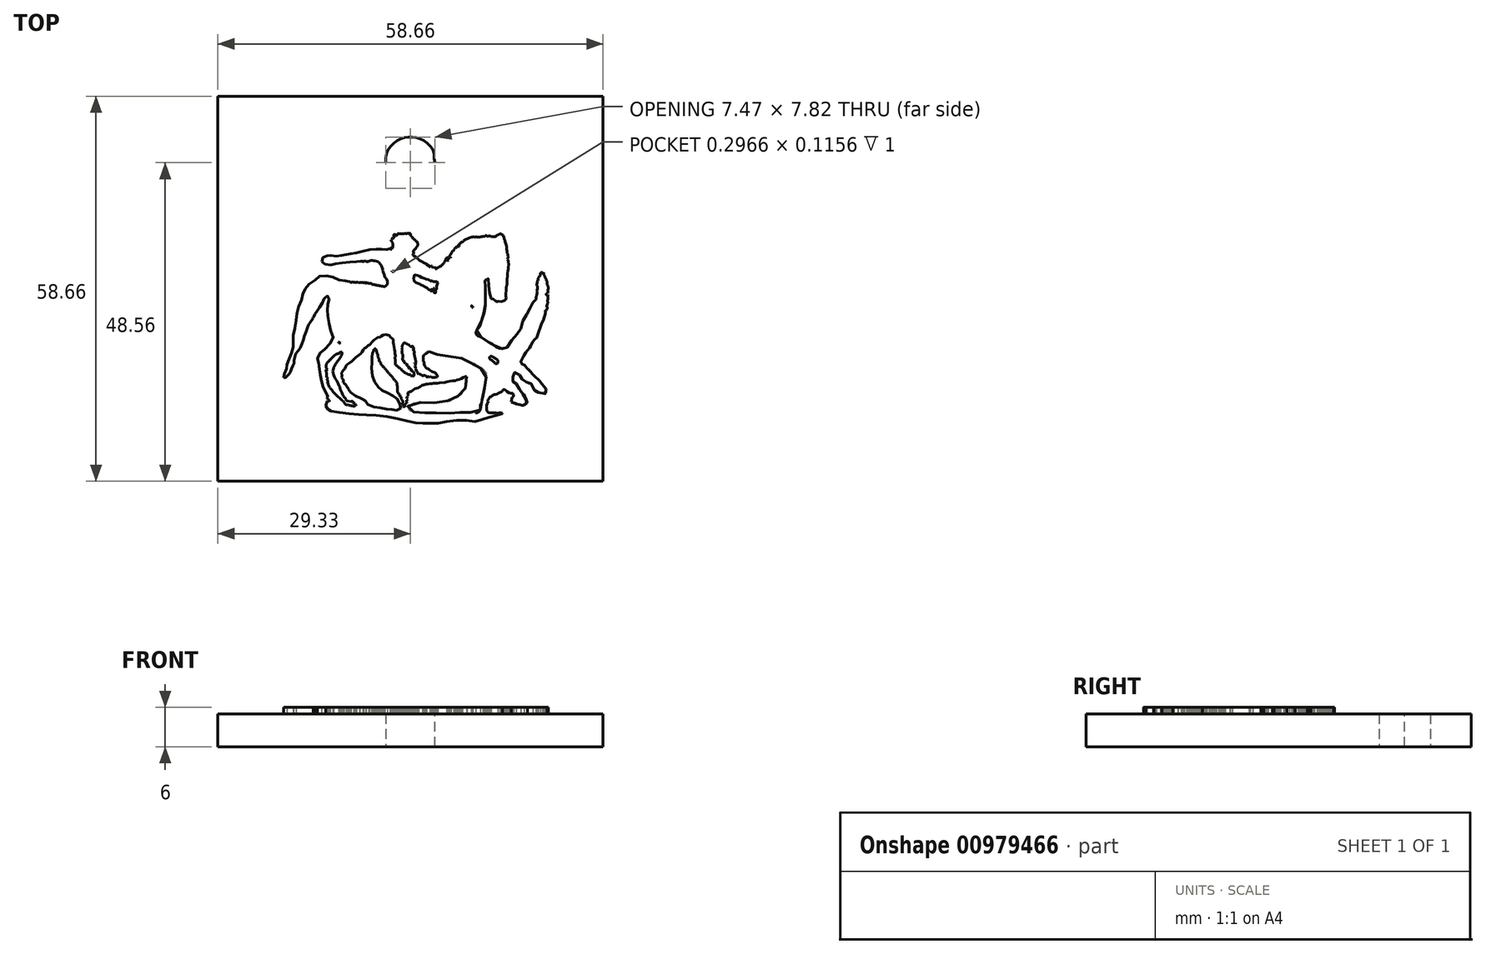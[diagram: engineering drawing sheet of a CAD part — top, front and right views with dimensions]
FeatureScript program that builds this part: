
annotation { "Feature Type Name" : "Feature", "Feature Type Description" : "" }
export const myFeature = defineFeature(function(context is Context, id is Id, definition is map)
    precondition{}
    {
        {
            var Q0;
            Q0=qCreatedBy(makeId("Top.planeOp"),FACE);
            var sketch = newSketch(context, id + "F0", { "sketchPlane" : qUnion([Q0])});
            skLineSegment(sketch, "E0", {"start": v(29.33, 29.33) * mm, "end": v(-29.33, 29.33) * mm});
            skLineSegment(sketch, "E1", {"start": v(-29.33, 29.33) * mm, "end": v(-29.33, -29.33) * mm});
            skLineSegment(sketch, "E2", {"start": v(-29.33, -29.33) * mm, "end": v(29.33, -29.33) * mm});
            skLineSegment(sketch, "E3", {"start": v(29.33, -29.33) * mm, "end": v(29.33, 29.33) * mm});
            skLineSegment(sketch, "E4", {"start": v(14, -19.04) * mm, "end": v(14, -19) * mm});
            skLineSegment(sketch, "E5", {"start": v(11.06, 7.86) * mm, "end": v(11.06, 8) * mm});
            skLineSegment(sketch, "E6", {"start": v(3.86, 3) * mm, "end": v(3.86, 3.18) * mm});
            skLineSegment(sketch, "E7", {"start": v(-7.23, 4.19) * mm, "end": v(-7.23, 4.11) * mm});
            skLineSegment(sketch, "E8", {"start": v(-7.15, 0.98) * mm, "end": v(-7.73, 0.98) * mm});
            skLineSegment(sketch, "E9", {"start": v(1.24, -12.84) * mm, "end": v(1.24, -13.05) * mm});
            skFitSpline(sketch, "E10", {"points": [v(3.73, 19.23) * mm, v(3.63, 18.57) * mm, v(3.43, 17.28) * mm, v(1.94, 15.85) * mm, v(0, 15.32) * mm, v(-1.96, 15.85) * mm, v(-3.38, 17.28) * mm, v(-3.73, 18.57) * mm, v(-3.73, 19.23) * mm, v(-3.73, 19.23) * mm]});
            skFitSpline(sketch, "E11", {"points": [v(-3.73, 19.23) * mm, v(-3.73, 19.89) * mm, v(-3.38, 21.18) * mm, v(-1.96, 22.61) * mm, v(0, 23.14) * mm, v(1.94, 22.61) * mm, v(3.43, 21.18) * mm, v(3.63, 19.89) * mm, v(3.73, 19.23) * mm]});
            skFitSpline(sketch, "E12", {"points": [v(-12.55, -16.47) * mm, v(-12.57, -16.49) * mm, v(-12.62, -16.51) * mm, v(-12.68, -16.56) * mm, v(-12.72, -16.58) * mm, v(-12.75, -16.6) * mm]});
            skFitSpline(sketch, "E13", {"points": [v(-12.75, -16.6) * mm, v(-12.72, -16.63) * mm, v(-12.67, -16.68) * mm, v(-12.6, -16.76) * mm, v(-12.56, -16.8) * mm, v(-12.54, -16.83) * mm]});
            skFitSpline(sketch, "E14", {"points": [v(-12.54, -16.83) * mm, v(-12.55, -16.85) * mm, v(-12.56, -16.88) * mm, v(-12.58, -16.92) * mm, v(-12.6, -16.95) * mm, v(-12.6, -16.96) * mm]});
            skFitSpline(sketch, "E15", {"points": [v(-12.6, -16.96) * mm, v(-12.57, -16.97) * mm, v(-12.5, -16.99) * mm, v(-12.41, -17) * mm, v(-12.35, -17.02) * mm, v(-12.31, -17.03) * mm]});
            skFitSpline(sketch, "E16", {"points": [v(-12.31, -17.03) * mm, v(-12.32, -17.06) * mm, v(-12.33, -17.11) * mm, v(-12.48, -17.1) * mm, v(-12.56, -17.07) * mm, v(-12.63, -17.05) * mm]});
            skFitSpline(sketch, "E17", {"points": [v(-12.63, -17.05) * mm, v(-12.69, -17.14) * mm, v(-12.8, -17.3) * mm, v(-12.87, -17.61) * mm, v(-12.9, -17.83) * mm, v(-12.87, -17.96) * mm, v(-12.85, -18) * mm, v(-12.8, -18.06) * mm, v(-12.74, -18.16) * mm, v(-12.65, -18.28) * mm, v(-12.58, -18.37) * mm, v(-12.53, -18.43) * mm, v(-12.51, -18.46) * mm, v(-12.43, -18.5) * mm, v(-12.26, -18.57) * mm, v(-12.04, -18.7) * mm, v(-11.65, -18.78) * mm, v(-11.1, -18.82) * mm, v(-10.4, -18.94) * mm, v(-9.72, -19.03) * mm, v(-9.05, -19.1) * mm, v(-8.38, -19.14) * mm, v(-7.79, -19.18) * mm, v(-7.27, -19.2) * mm, v(-6.82, -19.22) * mm, v(-6.25, -19.25) * mm, v(-5.58, -19.3) * mm, v(-4.8, -19.37) * mm, v(-3.99, -19.46) * mm, v(-3.15, -19.6) * mm, v(-2.29, -19.75) * mm, v(-1.49, -19.96) * mm, v(-0.74, -20.15) * mm, v(-0.04, -20.3) * mm, v(0.46, -20.43) * mm, v(0.78, -20.48) * mm, v(0.9, -20.48) * mm, v(1.22, -20.48) * mm, v(1.74, -20.48) * mm, v(2.46, -20.49) * mm, v(3, -20.49) * mm, v(3.37, -20.5) * mm, v(3.55, -20.52) * mm, v(3.84, -20.55) * mm, v(4.25, -20.53) * mm, v(4.75, -20.43) * mm, v(5.33, -20.3) * mm, v(6, -20.19) * mm, v(6.76, -20.06) * mm, v(7.48, -20.05) * mm, v(8.15, -20.07) * mm, v(8.78, -20.05) * mm, v(9.34, -20.14) * mm, v(9.82, -20.24) * mm, v(10.24, -20.2) * mm, v(10.61, -20.08) * mm, v(10.95, -19.92) * mm, v(11.28, -19.8) * mm, v(11.65, -19.68) * mm, v(12.08, -19.57) * mm, v(12.56, -19.46) * mm, v(12.98, -19.36) * mm, v(13.36, -19.25) * mm, v(13.68, -19.15) * mm, v(13.9, -19.08) * mm, v(14, -19.04) * mm]});
            skFitSpline(sketch, "E18", {"points": [v(14, -19) * mm, v(13.99, -19) * mm, v(13.96, -18.98) * mm, v(13.91, -18.96) * mm, v(13.72, -18.94) * mm, v(13.4, -18.96) * mm, v(12.92, -18.94) * mm, v(12.44, -18.94) * mm, v(11.97, -18.9) * mm, v(11.64, -18.53) * mm, v(11.59, -18.12) * mm, v(11.62, -17.76) * mm, v(11.73, -17.48) * mm, v(11.8, -17.3) * mm, v(11.84, -17.15) * mm, v(11.83, -17.1) * mm, v(11.86, -17.04) * mm, v(11.83, -17.04) * mm, v(11.81, -17.03) * mm, v(11.8, -17.03) * mm, v(11.8, -17.03) * mm]});
            skFitSpline(sketch, "E19", {"points": [v(11.8, -17.03) * mm, v(11.82, -16.98) * mm, v(11.88, -16.9) * mm, v(11.96, -16.75) * mm, v(12.04, -16.62) * mm, v(12.15, -16.52) * mm, v(12.25, -16.45) * mm, v(12.34, -16.38) * mm, v(12.4, -16.33) * mm, v(12.45, -16.29) * mm, v(12.5, -16.25) * mm, v(12.57, -16.21) * mm, v(12.65, -16.17) * mm, v(12.79, -16.15) * mm, v(12.97, -16.14) * mm, v(13.19, -16.04) * mm, v(13.4, -15.94) * mm, v(13.6, -15.86) * mm, v(13.77, -15.75) * mm, v(13.9, -15.7) * mm, v(13.99, -15.64) * mm, v(14, -15.6) * mm, v(14.03, -15.55) * mm, v(14.06, -15.47) * mm, v(14.14, -15.39) * mm, v(14.24, -15.35) * mm, v(14.34, -15.36) * mm, v(14.43, -15.41) * mm, v(14.57, -15.52) * mm, v(14.77, -15.7) * mm, v(15.05, -15.9) * mm, v(15.34, -15.94) * mm, v(15.58, -15.96) * mm, v(15.7, -16.15) * mm, v(15.7, -16.29) * mm, v(15.7, -16.37) * mm]});
            skFitSpline(sketch, "E20", {"points": [v(15.7, -16.37) * mm, v(15.7, -16.37) * mm, v(15.7, -16.37) * mm, v(15.68, -16.36) * mm, v(15.65, -16.35) * mm, v(15.65, -16.43) * mm, v(15.63, -16.48) * mm, v(15.61, -16.53) * mm, v(15.6, -16.56) * mm, v(15.59, -16.58) * mm, v(15.57, -16.6) * mm, v(15.54, -16.6) * mm, v(15.52, -16.6) * mm, v(15.5, -16.6) * mm, v(15.49, -16.6) * mm]});
            skFitSpline(sketch, "E21", {"points": [v(15.49, -16.6) * mm, v(15.47, -16.67) * mm, v(15.43, -16.82) * mm, v(15.38, -17.06) * mm, v(15.35, -17.21) * mm, v(15.33, -17.3) * mm]});
            skFitSpline(sketch, "E22", {"points": [v(15.33, -17.3) * mm, v(15.39, -17.3) * mm, v(15.51, -17.33) * mm, v(15.7, -17.36) * mm, v(15.92, -17.44) * mm, v(16.16, -17.57) * mm, v(16.46, -17.66) * mm, v(16.7, -17.7) * mm, v(16.91, -17.72) * mm, v(17.05, -17.76) * mm, v(17.2, -17.76) * mm, v(17.33, -17.72) * mm, v(17.44, -17.65) * mm, v(17.54, -17.61) * mm, v(17.58, -17.56) * mm, v(17.6, -17.54) * mm, v(17.62, -17.5) * mm, v(17.69, -17.46) * mm, v(17.76, -17.41) * mm, v(17.81, -17.34) * mm, v(17.8, -17.25) * mm, v(17.75, -17.17) * mm, v(17.68, -17.03) * mm, v(17.62, -16.82) * mm, v(17.51, -16.56) * mm, v(17.44, -16.36) * mm, v(17.38, -16.23) * mm, v(17.33, -16.16) * mm, v(17.2, -16.06) * mm, v(17, -15.92) * mm, v(16.8, -15.64) * mm, v(16.7, -15.42) * mm, v(16.61, -15.27) * mm, v(16.56, -15.2) * mm, v(16.44, -15.1) * mm, v(16.28, -14.98) * mm, v(16.1, -14.76) * mm, v(16.13, -14.55) * mm, v(16.07, -14.44) * mm, v(16.03, -14.41) * mm, v(15.95, -14.39) * mm, v(15.84, -14.4) * mm, v(15.73, -14.32) * mm, v(15.65, -14.24) * mm, v(15.6, -14.15) * mm, v(15.55, -14.08) * mm, v(15.48, -13.98) * mm, v(15.4, -13.84) * mm, v(15.42, -13.62) * mm, v(15.54, -13.49) * mm, v(15.64, -13.36) * mm, v(15.7, -13.24) * mm, v(15.76, -13.12) * mm, v(15.8, -13.01) * mm, v(15.82, -12.9) * mm, v(15.86, -12.78) * mm, v(15.96, -12.66) * mm, v(16.13, -12.63) * mm, v(16.31, -12.75) * mm, v(16.46, -12.95) * mm, v(16.66, -13.18) * mm, v(16.81, -13.35) * mm, v(16.9, -13.47) * mm, v(16.95, -13.55) * mm, v(16.97, -13.64) * mm, v(17, -13.72) * mm, v(17.06, -13.78) * mm, v(17.13, -13.82) * mm, v(17.2, -13.84) * mm, v(17.26, -13.88) * mm, v(17.37, -13.95) * mm, v(17.5, -14.07) * mm, v(17.68, -14.22) * mm, v(17.8, -14.34) * mm, v(17.91, -14.41) * mm, v(17.98, -14.44) * mm, v(18.14, -14.46) * mm, v(18.4, -14.47) * mm, v(18.63, -14.72) * mm, v(18.72, -14.96) * mm, v(18.78, -15.18) * mm, v(18.81, -15.35) * mm, v(18.84, -15.5) * mm, v(18.87, -15.6) * mm, v(18.93, -15.68) * mm, v(19.08, -15.72) * mm, v(19.3, -15.77) * mm, v(19.57, -15.86) * mm, v(19.82, -15.98) * mm, v(20.08, -16.07) * mm, v(20.36, -16.05) * mm, v(20.57, -16) * mm, v(20.75, -15.94) * mm, v(20.8, -15.8) * mm, v(20.8, -15.62) * mm, v(20.76, -15.41) * mm, v(20.61, -15.22) * mm, v(20.43, -15.1) * mm, v(20.25, -14.94) * mm, v(20.12, -14.75) * mm, v(20.05, -14.58) * mm, v(19.99, -14.45) * mm, v(19.92, -14.37) * mm, v(19.85, -14.27) * mm, v(19.76, -14.17) * mm, v(19.66, -14.05) * mm, v(19.57, -13.95) * mm, v(19.5, -13.87) * mm, v(19.43, -13.81) * mm, v(19.31, -13.7) * mm, v(19.16, -13.54) * mm, v(18.95, -13.34) * mm, v(18.73, -13.07) * mm, v(18.46, -12.76) * mm, v(18.11, -12.44) * mm, v(17.84, -12.18) * mm, v(17.64, -11.95) * mm, v(17.5, -11.78) * mm, v(17.4, -11.66) * mm, v(17.36, -11.6) * mm]});
            skFitSpline(sketch, "E23", {"points": [v(17.36, -11.6) * mm, v(17.3, -11.61) * mm, v(17.18, -11.64) * mm, v(17.03, -11.52) * mm, v(16.92, -11.39) * mm, v(16.83, -11.24) * mm, v(16.82, -11.07) * mm, v(16.87, -10.92) * mm, v(16.95, -10.8) * mm, v(17.03, -10.67) * mm, v(17.15, -10.48) * mm, v(17.3, -10.23) * mm, v(17.48, -9.9) * mm, v(17.6, -9.68) * mm, v(17.69, -9.54) * mm, v(17.71, -9.5) * mm, v(17.81, -9.42) * mm, v(17.98, -9.33) * mm, v(18.11, -9.1) * mm, v(18.22, -8.95) * mm, v(18.3, -8.86) * mm, v(18.32, -8.81) * mm, v(18.38, -8.66) * mm, v(18.47, -8.39) * mm, v(18.68, -8.06) * mm, v(18.84, -7.8) * mm, v(18.99, -7.66) * mm, v(19.08, -7.62) * mm, v(19.16, -7.57) * mm, v(19.21, -7.5) * mm, v(19.24, -7.44) * mm, v(19.28, -7.36) * mm, v(19.3, -7.24) * mm, v(19.34, -7.1) * mm, v(19.42, -6.86) * mm, v(19.55, -6.5) * mm, v(19.72, -6.01) * mm, v(19.86, -5.63) * mm, v(19.97, -5.36) * mm, v(20.06, -5.2) * mm, v(20.17, -5.03) * mm, v(20.27, -4.85) * mm, v(20.33, -4.63) * mm, v(20.36, -4.45) * mm, v(20.4, -4.29) * mm, v(20.46, -4.16) * mm, v(20.5, -4.04) * mm, v(20.56, -3.94) * mm, v(20.64, -3.82) * mm, v(20.54, -3.76) * mm, v(20.55, -3.7) * mm, v(20.56, -3.68) * mm, v(20.57, -3.64) * mm, v(20.58, -3.6) * mm, v(20.6, -3.58) * mm, v(20.58, -3.5) * mm, v(20.45, -3.42) * mm, v(20.6, -3.35) * mm, v(20.7, -3.3) * mm, v(20.75, -3.17) * mm, v(20.82, -3.08) * mm, v(20.87, -2.96) * mm, v(20.84, -2.85) * mm, v(20.77, -2.75) * mm, v(20.75, -2.68) * mm, v(20.74, -2.65) * mm]});
            skFitSpline(sketch, "E24", {"points": [v(20.74, -2.65) * mm, v(20.75, -2.6) * mm, v(20.78, -2.52) * mm, v(20.82, -2.4) * mm, v(20.84, -2.32) * mm, v(20.86, -2.27) * mm]});
            skFitSpline(sketch, "E25", {"points": [v(20.86, -2.27) * mm, v(20.87, -2.27) * mm, v(20.9, -2.26) * mm, v(20.93, -2.25) * mm, v(20.95, -2.24) * mm, v(20.96, -2.23) * mm]});
            skFitSpline(sketch, "E26", {"points": [v(20.96, -2.23) * mm, v(20.96, -2.22) * mm, v(20.95, -2.19) * mm, v(20.94, -2.15) * mm, v(20.93, -2.09) * mm, v(20.92, -2.01) * mm, v(20.9, -1.92) * mm, v(20.9, -1.8) * mm, v(20.93, -1.64) * mm, v(20.94, -1.46) * mm, v(20.97, -1.32) * mm, v(20.96, -1.22) * mm, v(20.94, -1.16) * mm, v(20.92, -1.1) * mm, v(20.92, -1.04) * mm, v(20.92, -0.97) * mm, v(20.92, -0.93) * mm, v(20.92, -0.9) * mm]});
            skFitSpline(sketch, "E27", {"points": [v(20.92, -0.9) * mm, v(20.91, -0.92) * mm, v(20.9, -0.95) * mm, v(20.87, -1) * mm, v(20.85, -1.02) * mm, v(20.85, -1.03) * mm]});
            skFitSpline(sketch, "E28", {"points": [v(20.85, -1.03) * mm, v(20.8, -1) * mm, v(20.73, -0.93) * mm, v(20.73, -0.77) * mm, v(20.78, -0.69) * mm, v(20.8, -0.64) * mm]});
            skFitSpline(sketch, "E29", {"points": [v(20.8, -0.64) * mm, v(20.82, -0.65) * mm, v(20.85, -0.65) * mm, v(20.9, -0.67) * mm, v(20.95, -0.68) * mm, v(20.97, -0.7) * mm]});
            skFitSpline(sketch, "E30", {"points": [v(20.97, -0.7) * mm, v(20.97, -0.66) * mm, v(20.97, -0.59) * mm, v(20.96, -0.48) * mm, v(20.96, -0.35) * mm, v(20.97, -0.2) * mm, v(20.99, -0.03) * mm, v(21, 0.11) * mm, v(21, 0.22) * mm, v(20.99, 0.29) * mm, v(20.94, 0.41) * mm, v(20.88, 0.6) * mm, v(20.83, 0.87) * mm, v(20.84, 1.07) * mm, v(20.8, 1.2) * mm, v(20.75, 1.24) * mm, v(20.72, 1.28) * mm, v(20.7, 1.3) * mm]});
            skFitSpline(sketch, "E31", {"points": [v(20.7, 1.3) * mm, v(20.7, 1.32) * mm, v(20.7, 1.37) * mm, v(20.67, 1.44) * mm, v(20.63, 1.56) * mm, v(20.55, 1.72) * mm, v(20.44, 1.93) * mm, v(20.39, 2.08) * mm, v(20.34, 2.16) * mm, v(20.32, 2.17) * mm, v(20.29, 2.22) * mm, v(20.36, 2.35) * mm, v(20.18, 2.38) * mm, v(20.14, 2.46) * mm, v(20.12, 2.5) * mm]});
            skFitSpline(sketch, "E32", {"points": [v(20.12, 2.5) * mm, v(20.1, 2.5) * mm, v(20.05, 2.49) * mm, v(19.97, 2.48) * mm, v(19.9, 2.46) * mm, v(19.86, 2.42) * mm, v(19.83, 2.38) * mm, v(19.8, 2.36) * mm, v(19.8, 2.34) * mm]});
            skFitSpline(sketch, "E33", {"points": [v(19.8, 2.34) * mm, v(19.8, 2.3) * mm, v(19.82, 2.2) * mm, v(19.77, 2.04) * mm, v(19.7, 1.94) * mm, v(19.63, 1.88) * mm, v(19.58, 1.83) * mm, v(19.55, 1.74) * mm, v(19.5, 1.63) * mm, v(19.42, 1.48) * mm, v(19.47, 1.37) * mm, v(19.5, 1.32) * mm]});
            skFitSpline(sketch, "E34", {"points": [v(19.5, 1.32) * mm, v(19.48, 1.3) * mm, v(19.45, 1.26) * mm, v(19.34, 1.22) * mm, v(19.4, 1.17) * mm, v(19.44, 1.14) * mm]});
            skFitSpline(sketch, "E35", {"points": [v(19.44, 1.14) * mm, v(19.4, 1.1) * mm, v(19.33, 1.02) * mm, v(19.29, 0.86) * mm, v(19.28, 0.73) * mm, v(19.26, 0.64) * mm, v(19.25, 0.58) * mm, v(19.25, 0.51) * mm, v(19.28, 0.44) * mm, v(19.33, 0.36) * mm, v(19.36, 0.24) * mm, v(19.35, 0.1) * mm, v(19.34, -0.07) * mm, v(19.33, -0.2) * mm, v(19.33, -0.29) * mm, v(19.33, -0.34) * mm, v(19.33, -0.4) * mm, v(19.33, -0.46) * mm, v(19.32, -0.53) * mm, v(19.3, -0.64) * mm, v(19.27, -0.77) * mm, v(19.24, -0.93) * mm, v(19.2, -1.05) * mm, v(19.2, -1.14) * mm, v(19.18, -1.18) * mm, v(19.16, -1.24) * mm, v(19.12, -1.29) * mm, v(19.09, -1.37) * mm, v(19.14, -1.44) * mm, v(19.16, -1.52) * mm, v(19.14, -1.58) * mm, v(19.12, -1.63) * mm, v(19.1, -1.65) * mm]});
            skFitSpline(sketch, "E36", {"points": [v(19.1, -1.65) * mm, v(19.08, -1.68) * mm, v(19.04, -1.73) * mm, v(18.96, -1.82) * mm, v(18.9, -1.9) * mm, v(18.84, -1.95) * mm, v(18.8, -2) * mm, v(18.75, -2.03) * mm, v(18.72, -2.06) * mm, v(18.7, -2.09) * mm, v(18.68, -2.15) * mm, v(18.7, -2.25) * mm, v(18.63, -2.36) * mm, v(18.52, -2.5) * mm, v(18.4, -2.7) * mm, v(18.26, -2.96) * mm, v(18.13, -3.19) * mm, v(18.01, -3.37) * mm, v(17.9, -3.52) * mm, v(17.8, -3.68) * mm, v(17.72, -3.85) * mm, v(17.64, -4.03) * mm, v(17.54, -4.22) * mm, v(17.42, -4.43) * mm, v(17.3, -4.65) * mm, v(17.17, -4.86) * mm, v(17.04, -5.06) * mm, v(16.96, -5.28) * mm, v(16.92, -5.53) * mm, v(16.9, -5.81) * mm, v(16.8, -6.12) * mm, v(16.62, -6.3) * mm, v(16.5, -6.44) * mm, v(16.46, -6.56) * mm, v(16.39, -6.69) * mm, v(16.28, -6.83) * mm, v(16.16, -7) * mm, v(15.98, -7.17) * mm, v(15.76, -7.37) * mm, v(15.56, -7.63) * mm, v(15.4, -7.94) * mm, v(15.25, -8.25) * mm, v(15.06, -8.54) * mm, v(14.92, -8.78) * mm, v(14.77, -8.92) * mm, v(14.63, -8.96) * mm, v(14.51, -9) * mm, v(14.4, -9.05) * mm, v(14.28, -9.07) * mm, v(14.18, -9.09) * mm, v(14.1, -9.1) * mm, v(14.02, -9.11) * mm, v(13.82, -9.1) * mm, v(13.51, -9.04) * mm, v(13.1, -8.88) * mm, v(12.83, -8.68) * mm, v(12.63, -8.54) * mm, v(12.5, -8.47) * mm, v(12.37, -8.4) * mm, v(12.25, -8.33) * mm, v(12.13, -8.27) * mm, v(11.92, -8.13) * mm, v(11.63, -7.93) * mm, v(11.23, -7.68) * mm, v(10.95, -7.47) * mm, v(10.75, -7.37) * mm, v(10.66, -7.34) * mm, v(10.44, -7.28) * mm, v(10.15, -7.08) * mm, v(9.98, -6.62) * mm, v(10.17, -6.2) * mm, v(10.46, -5.86) * mm, v(10.65, -5.47) * mm, v(10.8, -5.12) * mm, v(10.88, -4.81) * mm, v(10.94, -4.56) * mm, v(11.02, -4.26) * mm, v(11.12, -3.94) * mm, v(11.23, -3.58) * mm, v(11.32, -3.24) * mm, v(11.37, -2.92) * mm, v(11.4, -2.62) * mm, v(11.44, -2.24) * mm, v(11.46, -1.76) * mm, v(11.42, -1.19) * mm, v(11.4, -0.76) * mm, v(11.43, -0.49) * mm, v(11.46, -0.36) * mm, v(11.47, -0.21) * mm, v(11.47, -0.05) * mm, v(11.46, 0.14) * mm, v(11.44, 0.33) * mm, v(11.41, 0.54) * mm, v(11.38, 0.76) * mm, v(11.35, 0.95) * mm, v(11.34, 1.1) * mm, v(11.33, 1.23) * mm, v(11.32, 1.36) * mm, v(11.34, 1.5) * mm, v(11.43, 1.64) * mm, v(11.57, 1.7) * mm, v(11.71, 1.68) * mm, v(11.83, 1.57) * mm, v(11.87, 1.4) * mm, v(11.88, 1.2) * mm, v(11.89, 1) * mm, v(11.9, 0.8) * mm, v(11.93, 0.64) * mm, v(11.97, 0.5) * mm, v(12, 0.3) * mm, v(12, 0.05) * mm, v(12.02, -0.25) * mm, v(12.04, -0.53) * mm, v(12.09, -0.78) * mm, v(12.14, -1) * mm, v(12.18, -1.18) * mm, v(12.22, -1.32) * mm, v(12.27, -1.43) * mm, v(12.3, -1.5) * mm, v(12.3, -1.55) * mm]});
            skFitSpline(sketch, "E37", {"points": [v(12.3, -1.55) * mm, v(12.4, -1.56) * mm, v(12.57, -1.57) * mm, v(12.8, -1.72) * mm, v(12.95, -1.86) * mm, v(13.07, -1.96) * mm, v(13.16, -1.98) * mm, v(13.25, -1.95) * mm, v(13.34, -1.92) * mm, v(13.42, -1.9) * mm, v(13.56, -1.93) * mm, v(13.74, -1.96) * mm, v(13.96, -1.92) * mm, v(14.15, -1.87) * mm, v(14.3, -1.83) * mm, v(14.4, -1.75) * mm, v(14.46, -1.65) * mm, v(14.52, -1.54) * mm, v(14.57, -1.43) * mm, v(14.58, -1.32) * mm, v(14.55, -1.23) * mm, v(14.52, -1.16) * mm, v(14.51, -0.98) * mm, v(14.55, -0.71) * mm, v(14.56, -0.35) * mm, v(14.6, 0) * mm, v(14.64, 0.32) * mm, v(14.69, 0.63) * mm, v(14.73, 0.89) * mm, v(14.74, 1.11) * mm, v(14.73, 1.3) * mm, v(14.74, 1.52) * mm, v(14.76, 1.77) * mm, v(14.78, 2.05) * mm, v(14.8, 2.3) * mm, v(14.82, 2.5) * mm, v(14.84, 2.67) * mm, v(14.86, 2.81) * mm, v(14.88, 2.93) * mm, v(14.9, 3.03) * mm, v(14.9, 3.15) * mm, v(14.92, 3.3) * mm, v(14.95, 3.5) * mm, v(14.95, 3.7) * mm, v(14.92, 3.93) * mm, v(14.87, 4.18) * mm, v(14.85, 4.34) * mm, v(14.83, 4.43) * mm]});
            skFitSpline(sketch, "E38", {"points": [v(14.83, 4.43) * mm, v(14.84, 4.44) * mm, v(14.86, 4.46) * mm, v(14.89, 4.5) * mm, v(14.91, 4.52) * mm, v(14.92, 4.54) * mm]});
            skFitSpline(sketch, "E39", {"points": [v(14.92, 4.54) * mm, v(14.9, 4.54) * mm, v(14.87, 4.55) * mm, v(14.82, 4.57) * mm, v(14.78, 4.57) * mm, v(14.77, 4.58) * mm]});
            skFitSpline(sketch, "E40", {"points": [v(14.77, 4.58) * mm, v(14.78, 4.59) * mm, v(14.8, 4.6) * mm, v(14.81, 4.64) * mm, v(14.85, 4.69) * mm, v(14.9, 4.77) * mm, v(14.87, 4.88) * mm, v(14.81, 4.92) * mm, v(14.78, 4.94) * mm]});
            skFitSpline(sketch, "E41", {"points": [v(14.78, 4.94) * mm, v(14.8, 5) * mm, v(14.84, 5.12) * mm, v(14.82, 5.3) * mm, v(14.73, 5.43) * mm, v(14.7, 5.55) * mm, v(14.72, 5.63) * mm, v(14.73, 5.75) * mm, v(14.7, 5.9) * mm, v(14.68, 6.08) * mm, v(14.68, 6.28) * mm, v(14.65, 6.5) * mm, v(14.57, 6.75) * mm, v(14.51, 6.94) * mm, v(14.47, 7.09) * mm, v(14.44, 7.18) * mm, v(14.43, 7.28) * mm, v(14.4, 7.39) * mm, v(14.34, 7.49) * mm, v(14.31, 7.56) * mm, v(14.28, 7.6) * mm, v(14.27, 7.6) * mm, v(14.23, 7.67) * mm, v(14.29, 7.81) * mm, v(14.15, 7.96) * mm, v(14.13, 8.08) * mm, v(14.1, 8.15) * mm, v(14.09, 8.17) * mm, v(14.04, 8.2) * mm, v(13.95, 8.25) * mm, v(13.82, 8.3) * mm, v(13.76, 8.38) * mm, v(13.7, 8.41) * mm, v(13.66, 8.41) * mm, v(13.63, 8.41) * mm, v(13.62, 8.41) * mm]});
            skFitSpline(sketch, "E42", {"points": [v(13.62, 8.41) * mm, v(13.6, 8.37) * mm, v(13.57, 8.3) * mm, v(13.45, 8.27) * mm, v(13.33, 8.23) * mm, v(13.23, 8.17) * mm, v(13.12, 8.1) * mm, v(13.07, 8) * mm, v(12.96, 7.94) * mm, v(12.85, 7.95) * mm, v(12.75, 7.94) * mm, v(12.67, 7.94) * mm, v(12.62, 7.94) * mm, v(12.54, 7.93) * mm, v(12.43, 7.92) * mm, v(12.31, 8.01) * mm, v(12.3, 8.1) * mm, v(12.29, 8.15) * mm]});
            skFitSpline(sketch, "E43", {"points": [v(12.29, 8.15) * mm, v(12.27, 8.13) * mm, v(12.23, 8.09) * mm, v(12.17, 8.02) * mm, v(12.13, 7.98) * mm, v(12.11, 7.95) * mm]});
            skFitSpline(sketch, "E44", {"points": [v(12.11, 7.95) * mm, v(12.09, 7.99) * mm, v(12.04, 8.05) * mm, v(11.91, 8.06) * mm, v(11.85, 8) * mm, v(11.79, 7.98) * mm, v(11.76, 7.99) * mm, v(11.7, 8.01) * mm, v(11.63, 8.05) * mm, v(11.54, 8.1) * mm, v(11.48, 8.13) * mm, v(11.45, 8.15) * mm]});
            skFitSpline(sketch, "E45", {"points": [v(11.45, 8.15) * mm, v(11.44, 8.1) * mm, v(11.43, 8.03) * mm, v(11.31, 7.98) * mm, v(11.25, 8.03) * mm, v(11.21, 8.05) * mm]});
            skFitSpline(sketch, "E46", {"points": [v(11.21, 8.05) * mm, v(11.2, 8.03) * mm, v(11.17, 8) * mm, v(11.12, 7.93) * mm, v(11.08, 7.89) * mm, v(11.06, 7.86) * mm]});
            skFitSpline(sketch, "E47", {"points": [v(11.06, 8) * mm, v(11.02, 8) * mm, v(10.93, 7.95) * mm, v(10.8, 7.97) * mm, v(10.7, 7.9) * mm, v(10.62, 7.88) * mm, v(10.57, 7.9) * mm, v(10.5, 7.9) * mm, v(10.44, 7.89) * mm, v(10.38, 7.88) * mm, v(10.33, 7.87) * mm, v(10.28, 7.87) * mm, v(10.25, 7.87) * mm, v(10.2, 7.9) * mm, v(10.13, 7.92) * mm, v(10.03, 7.94) * mm, v(9.97, 7.9) * mm, v(9.91, 7.87) * mm, v(9.88, 7.88) * mm, v(9.8, 7.9) * mm, v(9.69, 7.9) * mm, v(9.53, 7.92) * mm, v(9.43, 7.87) * mm, v(9.37, 7.85) * mm, v(9.34, 7.86) * mm, v(9.24, 7.86) * mm, v(9.06, 7.81) * mm, v(8.8, 7.72) * mm, v(8.63, 7.6) * mm, v(8.48, 7.53) * mm, v(8.37, 7.5) * mm, v(8.29, 7.47) * mm, v(8.23, 7.44) * mm, v(8.2, 7.42) * mm, v(8.18, 7.4) * mm, v(8.15, 7.36) * mm, v(8.12, 7.33) * mm, v(8.08, 7.28) * mm, v(8.03, 7.24) * mm, v(7.96, 7.18) * mm, v(7.92, 7.15) * mm, v(7.9, 7.13) * mm]});
            skFitSpline(sketch, "E48", {"points": [v(7.9, 7.13) * mm, v(7.9, 7.12) * mm, v(7.9, 7.11) * mm, v(7.91, 7.1) * mm, v(7.93, 7.06) * mm, v(7.87, 7.1) * mm, v(7.84, 7.12) * mm, v(7.8, 7.14) * mm, v(7.8, 7.14) * mm]});
            skFitSpline(sketch, "E49", {"points": [v(7.8, 7.14) * mm, v(7.77, 7.13) * mm, v(7.73, 7.1) * mm, v(7.67, 7.05) * mm, v(7.63, 6.99) * mm, v(7.63, 6.9) * mm, v(7.56, 6.91) * mm, v(7.53, 6.9) * mm, v(7.51, 6.9) * mm]});
            skFitSpline(sketch, "E50", {"points": [v(7.51, 6.9) * mm, v(7.5, 6.86) * mm, v(7.47, 6.75) * mm, v(7.44, 6.6) * mm, v(7.41, 6.49) * mm, v(7.4, 6.44) * mm]});
            skFitSpline(sketch, "E51", {"points": [v(7.4, 6.44) * mm, v(7.4, 6.44) * mm, v(7.38, 6.44) * mm, v(7.36, 6.44) * mm, v(7.34, 6.44) * mm, v(7.33, 6.44) * mm]});
            skFitSpline(sketch, "E52", {"points": [v(7.33, 6.44) * mm, v(7.33, 6.46) * mm, v(7.32, 6.5) * mm, v(7.3, 6.56) * mm, v(7.31, 6.64) * mm, v(7.28, 6.63) * mm, v(7.28, 6.63) * mm, v(7.26, 6.63) * mm, v(7.27, 6.6) * mm, v(7.26, 6.57) * mm, v(7.26, 6.55) * mm, v(7.25, 6.54) * mm]});
            skFitSpline(sketch, "E53", {"points": [v(7.25, 6.54) * mm, v(7.24, 6.53) * mm, v(7.21, 6.53) * mm, v(7.18, 6.53) * mm, v(7.15, 6.53) * mm, v(7.14, 6.53) * mm]});
            skFitSpline(sketch, "E54", {"points": [v(7.14, 6.53) * mm, v(7.12, 6.46) * mm, v(7.09, 6.32) * mm, v(6.88, 6.27) * mm, v(6.79, 6.19) * mm, v(6.74, 6.14) * mm]});
            skFitSpline(sketch, "E55", {"points": [v(6.74, 6.14) * mm, v(6.74, 6.14) * mm, v(6.74, 6.12) * mm, v(6.75, 6.08) * mm, v(6.75, 6.06) * mm, v(6.76, 6.04) * mm]});
            skFitSpline(sketch, "E56", {"points": [v(6.76, 6.04) * mm, v(6.74, 6.04) * mm, v(6.7, 6.05) * mm, v(6.64, 6.05) * mm, v(6.6, 6.06) * mm, v(6.58, 6.06) * mm]});
            skFitSpline(sketch, "E57", {"points": [v(6.58, 6.06) * mm, v(6.6, 6.04) * mm, v(6.62, 6.01) * mm, v(6.65, 5.97) * mm, v(6.67, 5.94) * mm, v(6.68, 5.92) * mm]});
            skFitSpline(sketch, "E58", {"points": [v(6.68, 5.92) * mm, v(6.64, 5.89) * mm, v(6.56, 5.81) * mm, v(6.44, 5.7) * mm, v(6.35, 5.62) * mm, v(6.3, 5.58) * mm]});
            skFitSpline(sketch, "E59", {"points": [v(6.3, 5.58) * mm, v(6.3, 5.53) * mm, v(6.3, 5.46) * mm, v(6.23, 5.37) * mm, v(6.17, 5.37) * mm, v(6.14, 5.37) * mm]});
            skFitSpline(sketch, "E60", {"points": [v(6.14, 5.37) * mm, v(6.14, 5.32) * mm, v(6.14, 5.22) * mm, v(6.02, 5.12) * mm, v(6, 5.03) * mm, v(5.98, 4.98) * mm]});
            skFitSpline(sketch, "E61", {"points": [v(5.98, 4.98) * mm, v(6, 4.98) * mm, v(6.03, 4.97) * mm, v(6.1, 4.94) * mm, v(6.14, 4.93) * mm, v(6.16, 4.92) * mm]});
            skFitSpline(sketch, "E62", {"points": [v(6.16, 4.92) * mm, v(6.15, 4.9) * mm, v(6.13, 4.85) * mm, v(6.1, 4.78) * mm, v(6.08, 4.73) * mm, v(6.07, 4.7) * mm]});
            skFitSpline(sketch, "E63", {"points": [v(6.07, 4.7) * mm, v(6.05, 4.73) * mm, v(6.02, 4.78) * mm, v(5.97, 4.85) * mm, v(5.94, 4.9) * mm, v(5.92, 4.92) * mm]});
            skFitSpline(sketch, "E64", {"points": [v(5.92, 4.92) * mm, v(5.92, 4.85) * mm, v(5.93, 4.71) * mm, v(5.83, 4.54) * mm, v(5.75, 4.44) * mm, v(5.7, 4.4) * mm]});
            skFitSpline(sketch, "E65", {"points": [v(5.7, 4.4) * mm, v(5.72, 4.39) * mm, v(5.75, 4.37) * mm, v(5.8, 4.33) * mm, v(5.82, 4.31) * mm, v(5.83, 4.3) * mm]});
            skFitSpline(sketch, "E66", {"points": [v(5.83, 4.3) * mm, v(5.76, 4.3) * mm, v(5.65, 4.28) * mm, v(5.55, 4.44) * mm, v(5.66, 4.53) * mm, v(5.68, 4.63) * mm, v(5.67, 4.7) * mm, v(5.66, 4.75) * mm, v(5.66, 4.78) * mm]});
            skFitSpline(sketch, "E67", {"points": [v(5.66, 4.78) * mm, v(5.6, 4.73) * mm, v(5.48, 4.63) * mm, v(5.38, 4.43) * mm, v(5.28, 4.2) * mm, v(5.14, 3.98) * mm, v(4.95, 3.76) * mm, v(4.8, 3.57) * mm, v(4.63, 3.44) * mm, v(4.48, 3.38) * mm, v(4.35, 3.31) * mm, v(4.24, 3.25) * mm, v(4.15, 3.2) * mm, v(4.09, 3.17) * mm, v(4.06, 3.15) * mm]});
            skFitSpline(sketch, "E68", {"points": [v(4.06, 3.15) * mm, v(4.07, 3.14) * mm, v(4.08, 3.13) * mm, v(4.1, 3.1) * mm, v(4.13, 3.08) * mm, v(4.13, 3.07) * mm]});
            skFitSpline(sketch, "E69", {"points": [v(4.13, 3.07) * mm, v(4.1, 3.08) * mm, v(4.04, 3.1) * mm, v(3.9, 3.14) * mm, v(3.9, 3.04) * mm, v(3.9, 2.98) * mm]});
            skFitSpline(sketch, "E70", {"points": [v(3.9, 2.98) * mm, v(3.9, 2.98) * mm, v(3.89, 2.99) * mm, v(3.87, 2.99) * mm, v(3.86, 3) * mm, v(3.86, 3) * mm]});
            skFitSpline(sketch, "E71", {"points": [v(3.86, 3.18) * mm, v(3.85, 3.19) * mm, v(3.82, 3.2) * mm, v(3.77, 3.23) * mm, v(3.73, 3.25) * mm, v(3.7, 3.26) * mm]});
            skFitSpline(sketch, "E72", {"points": [v(3.7, 3.26) * mm, v(3.7, 3.26) * mm, v(3.68, 3.24) * mm, v(3.65, 3.2) * mm, v(3.62, 3.18) * mm, v(3.6, 3.17) * mm]});
            skFitSpline(sketch, "E73", {"points": [v(3.6, 3.17) * mm, v(3.6, 3.19) * mm, v(3.59, 3.22) * mm, v(3.57, 3.27) * mm, v(3.55, 3.3) * mm, v(3.55, 3.33) * mm]});
            skFitSpline(sketch, "E74", {"points": [v(3.55, 3.33) * mm, v(3.53, 3.31) * mm, v(3.5, 3.29) * mm, v(3.46, 3.25) * mm, v(3.43, 3.23) * mm, v(3.42, 3.21) * mm]});
            skFitSpline(sketch, "E75", {"points": [v(3.42, 3.21) * mm, v(3.42, 3.23) * mm, v(3.43, 3.26) * mm, v(3.43, 3.3) * mm, v(3.44, 3.33) * mm, v(3.44, 3.34) * mm]});
            skFitSpline(sketch, "E76", {"points": [v(3.44, 3.34) * mm, v(3.41, 3.34) * mm, v(3.37, 3.32) * mm, v(3.25, 3.33) * mm, v(3.28, 3.42) * mm, v(3.3, 3.48) * mm]});
            skFitSpline(sketch, "E77", {"points": [v(3.3, 3.48) * mm, v(3.3, 3.48) * mm, v(3.28, 3.48) * mm, v(3.26, 3.48) * mm, v(3.24, 3.48) * mm, v(3.24, 3.48) * mm]});
            skFitSpline(sketch, "E78", {"points": [v(3.24, 3.48) * mm, v(3.22, 3.46) * mm, v(3.2, 3.42) * mm, v(3.14, 3.36) * mm, v(3.11, 3.32) * mm, v(3.1, 3.3) * mm]});
            skFitSpline(sketch, "E79", {"points": [v(3.1, 3.3) * mm, v(3.02, 3.34) * mm, v(2.87, 3.44) * mm, v(2.63, 3.59) * mm, v(2.48, 3.69) * mm, v(2.4, 3.74) * mm]});
            skFitSpline(sketch, "E80", {"points": [v(2.4, 3.74) * mm, v(2.4, 3.75) * mm, v(2.42, 3.78) * mm, v(2.43, 3.8) * mm, v(2.46, 3.85) * mm, v(2.42, 3.83) * mm, v(2.4, 3.82) * mm, v(2.34, 3.82) * mm, v(2.26, 3.86) * mm, v(2.13, 3.9) * mm, v(2, 3.98) * mm, v(1.84, 4.1) * mm, v(1.62, 4.17) * mm, v(1.46, 4.28) * mm, v(1.33, 4.37) * mm, v(1.23, 4.44) * mm, v(1.18, 4.54) * mm, v(1.13, 4.63) * mm, v(1.05, 4.67) * mm, v(0.97, 4.72) * mm, v(0.87, 4.78) * mm, v(0.76, 4.85) * mm, v(0.7, 4.9) * mm, v(0.65, 4.91) * mm]});
            skFitSpline(sketch, "E81", {"points": [v(0.65, 4.91) * mm, v(0.66, 4.93) * mm, v(0.66, 4.95) * mm, v(0.67, 5) * mm, v(0.68, 5.05) * mm, v(0.69, 5.07) * mm]});
            skFitSpline(sketch, "E82", {"points": [v(0.69, 5.07) * mm, v(0.66, 5.04) * mm, v(0.61, 4.98) * mm, v(0.5, 5) * mm, v(0.46, 5.07) * mm, v(0.4, 5.14) * mm, v(0.36, 5.21) * mm, v(0.33, 5.26) * mm, v(0.31, 5.3) * mm]});
            skFitSpline(sketch, "E83", {"points": [v(0.31, 5.3) * mm, v(0.33, 5.3) * mm, v(0.37, 5.3) * mm, v(0.43, 5.32) * mm, v(0.46, 5.33) * mm, v(0.48, 5.33) * mm]});
            skFitSpline(sketch, "E84", {"points": [v(0.48, 5.33) * mm, v(0.48, 5.35) * mm, v(0.48, 5.38) * mm, v(0.47, 5.44) * mm, v(0.48, 5.5) * mm, v(0.5, 5.55) * mm, v(0.5, 5.62) * mm, v(0.45, 5.66) * mm, v(0.45, 5.73) * mm, v(0.47, 5.8) * mm, v(0.57, 5.92) * mm, v(0.76, 6.06) * mm, v(0.93, 6.34) * mm, v(1.1, 6.54) * mm, v(1.17, 6.74) * mm, v(1.12, 6.89) * mm, v(1.08, 7) * mm, v(1.05, 7.09) * mm, v(1.02, 7.15) * mm, v(1, 7.2) * mm, v(1, 7.22) * mm]});
            skFitSpline(sketch, "E85", {"points": [v(1, 7.22) * mm, v(0.99, 7.2) * mm, v(0.98, 7.2) * mm, v(0.97, 7.17) * mm, v(0.97, 7.15) * mm, v(0.96, 7.14) * mm]});
            skFitSpline(sketch, "E86", {"points": [v(0.96, 7.14) * mm, v(0.9, 7.2) * mm, v(0.8, 7.33) * mm, v(0.63, 7.53) * mm, v(0.47, 7.58) * mm, v(0.39, 7.6) * mm]});
            skFitSpline(sketch, "E87", {"points": [v(0.39, 7.6) * mm, v(0.4, 7.62) * mm, v(0.42, 7.65) * mm, v(0.46, 7.7) * mm, v(0.48, 7.74) * mm, v(0.5, 7.76) * mm]});
            skFitSpline(sketch, "E88", {"points": [v(0.5, 7.76) * mm, v(0.46, 7.75) * mm, v(0.39, 7.74) * mm, v(0.28, 7.79) * mm, v(0.23, 7.9) * mm, v(0.17, 8) * mm, v(0.08, 8.08) * mm, v(0.02, 8.15) * mm, v(-0.01, 8.18) * mm]});
            skFitSpline(sketch, "E89", {"points": [v(-0.01, 8.18) * mm, v(0, 8.2) * mm, v(0.01, 8.24) * mm, v(0.04, 8.3) * mm, v(0.05, 8.36) * mm, v(0.06, 8.38) * mm]});
            skFitSpline(sketch, "E90", {"points": [v(0.06, 8.38) * mm, v(-0.01, 8.4) * mm, v(-0.18, 8.47) * mm, v(-0.45, 8.46) * mm, v(-0.61, 8.39) * mm, v(-0.69, 8.35) * mm]});
            skFitSpline(sketch, "E91", {"points": [v(-0.69, 8.35) * mm, v(-0.72, 8.4) * mm, v(-0.78, 8.46) * mm, v(-0.91, 8.41) * mm, v(-1.03, 8.38) * mm, v(-1.18, 8.38) * mm, v(-1.33, 8.35) * mm, v(-1.46, 8.39) * mm, v(-1.57, 8.4) * mm, v(-1.67, 8.39) * mm, v(-1.74, 8.38) * mm, v(-1.77, 8.37) * mm]});
            skFitSpline(sketch, "E92", {"points": [v(-1.77, 8.37) * mm, v(-1.78, 8.38) * mm, v(-1.78, 8.4) * mm, v(-1.79, 8.45) * mm, v(-1.8, 8.49) * mm, v(-1.8, 8.5) * mm]});
            skFitSpline(sketch, "E93", {"points": [v(-1.8, 8.5) * mm, v(-1.82, 8.47) * mm, v(-1.87, 8.4) * mm, v(-1.93, 8.3) * mm, v(-2, 8.22) * mm, v(-2.03, 8.15) * mm, v(-2.1, 8.12) * mm, v(-2.15, 8.19) * mm, v(-2.2, 8.24) * mm, v(-2.25, 8.29) * mm, v(-2.29, 8.32) * mm, v(-2.3, 8.33) * mm]});
            skFitSpline(sketch, "E94", {"points": [v(-2.3, 8.33) * mm, v(-2.32, 8.33) * mm, v(-2.36, 8.31) * mm, v(-2.42, 8.29) * mm, v(-2.47, 8.27) * mm, v(-2.5, 8.26) * mm]});
            skFitSpline(sketch, "E95", {"points": [v(-2.5, 8.26) * mm, v(-2.52, 8.22) * mm, v(-2.56, 8.14) * mm, v(-2.47, 8.02) * mm, v(-2.4, 8) * mm, v(-2.35, 7.99) * mm]});
            skFitSpline(sketch, "E96", {"points": [v(-2.35, 7.99) * mm, v(-2.38, 7.96) * mm, v(-2.44, 7.9) * mm, v(-2.54, 7.82) * mm, v(-2.6, 7.76) * mm, v(-2.63, 7.74) * mm]});
            skFitSpline(sketch, "E97", {"points": [v(-2.63, 7.74) * mm, v(-2.63, 7.73) * mm, v(-2.62, 7.72) * mm, v(-2.61, 7.7) * mm, v(-2.6, 7.68) * mm, v(-2.65, 7.72) * mm, v(-2.68, 7.73) * mm, v(-2.7, 7.74) * mm, v(-2.72, 7.75) * mm]});
            skFitSpline(sketch, "E98", {"points": [v(-2.72, 7.75) * mm, v(-2.74, 7.73) * mm, v(-2.77, 7.7) * mm, v(-2.82, 7.63) * mm, v(-2.86, 7.6) * mm, v(-2.88, 7.57) * mm]});
            skFitSpline(sketch, "E99", {"points": [v(-2.88, 7.57) * mm, v(-2.87, 7.56) * mm, v(-2.86, 7.54) * mm, v(-2.85, 7.51) * mm, v(-2.83, 7.49) * mm, v(-2.83, 7.48) * mm]});
            skFitSpline(sketch, "E100", {"points": [v(-2.83, 7.48) * mm, v(-2.87, 7.45) * mm, v(-2.94, 7.42) * mm, v(-2.94, 7.28) * mm, v(-2.82, 7.17) * mm, v(-2.73, 7) * mm, v(-2.68, 6.79) * mm, v(-2.7, 6.63) * mm, v(-2.7, 6.5) * mm, v(-2.69, 6.42) * mm, v(-2.68, 6.36) * mm, v(-2.67, 6.33) * mm]});
            skFitSpline(sketch, "E101", {"points": [v(-2.67, 6.33) * mm, v(-2.68, 6.32) * mm, v(-2.7, 6.3) * mm, v(-2.72, 6.26) * mm, v(-2.74, 6.22) * mm, v(-2.76, 6.2) * mm]});
            skFitSpline(sketch, "E102", {"points": [v(-2.76, 6.2) * mm, v(-2.76, 6.24) * mm, v(-2.79, 6.3) * mm, v(-2.95, 6.21) * mm, v(-3.03, 6.14) * mm, v(-3.1, 6.1) * mm]});
            skFitSpline(sketch, "E103", {"points": [v(-3.1, 6.1) * mm, v(-3.07, 6.1) * mm, v(-3.02, 6.12) * mm, v(-2.95, 6.14) * mm, v(-2.9, 6.16) * mm, v(-2.88, 6.16) * mm]});
            skFitSpline(sketch, "E104", {"points": [v(-2.88, 6.16) * mm, v(-2.87, 6.14) * mm, v(-2.85, 6.1) * mm, v(-2.82, 6.02) * mm, v(-2.8, 5.97) * mm, v(-2.8, 5.94) * mm]});
            skFitSpline(sketch, "E105", {"points": [v(-2.8, 5.94) * mm, v(-2.8, 5.94) * mm, v(-2.85, 5.94) * mm, v(-2.9, 5.94) * mm, v(-2.97, 5.94) * mm, v(-3.04, 6) * mm, v(-3.17, 6.1) * mm, v(-3.23, 5.95) * mm, v(-3.29, 5.97) * mm, v(-3.31, 5.99) * mm, v(-3.4, 6) * mm, v(-3.56, 5.97) * mm, v(-3.76, 6.03) * mm, v(-3.98, 6.04) * mm, v(-4.2, 6.02) * mm, v(-4.42, 6.01) * mm, v(-4.67, 6) * mm, v(-4.95, 6) * mm, v(-5.26, 6.01) * mm, v(-5.62, 6) * mm, v(-6.03, 5.95) * mm, v(-6.49, 5.91) * mm, v(-6.94, 5.79) * mm, v(-7.4, 5.67) * mm, v(-7.87, 5.62) * mm, v(-8.24, 5.49) * mm, v(-8.53, 5.38) * mm, v(-8.76, 5.36) * mm, v(-8.98, 5.34) * mm, v(-9.2, 5.32) * mm, v(-9.42, 5.33) * mm, v(-9.64, 5.27) * mm, v(-9.85, 5.21) * mm, v(-10.07, 5.22) * mm, v(-10.26, 5.17) * mm, v(-10.43, 5.1) * mm, v(-10.58, 5.06) * mm, v(-10.8, 5.02) * mm, v(-11.1, 4.99) * mm, v(-11.46, 4.94) * mm, v(-11.77, 5.01) * mm, v(-12.03, 5.08) * mm, v(-12.25, 5.1) * mm, v(-12.43, 5.1) * mm, v(-12.57, 5.08) * mm, v(-12.65, 5.03) * mm, v(-12.75, 4.98) * mm, v(-12.86, 4.94) * mm, v(-12.98, 4.89) * mm, v(-13.16, 4.85) * mm, v(-13.37, 4.74) * mm, v(-13.53, 4.5) * mm, v(-13.55, 4.27) * mm, v(-13.47, 4.13) * mm, v(-13.4, 4.05) * mm, v(-13.33, 3.95) * mm, v(-13.25, 3.85) * mm, v(-13.13, 3.81) * mm, v(-12.93, 3.75) * mm, v(-12.66, 3.66) * mm, v(-12.3, 3.64) * mm, v(-12, 3.65) * mm, v(-11.76, 3.7) * mm, v(-11.58, 3.75) * mm, v(-11.34, 3.8) * mm, v(-11.04, 3.86) * mm, v(-10.67, 3.93) * mm, v(-10.21, 3.99) * mm, v(-9.68, 4.03) * mm, v(-9.07, 4.08) * mm, v(-8.58, 4.12) * mm, v(-8.23, 4.14) * mm, v(-8.01, 4.15) * mm, v(-7.84, 4.15) * mm, v(-7.72, 4.16) * mm, v(-7.64, 4.18) * mm, v(-7.59, 4.2) * mm, v(-7.54, 4.2) * mm, v(-7.52, 4.2) * mm, v(-7.47, 4.2) * mm, v(-7.41, 4.2) * mm, v(-7.33, 4.2) * mm, v(-7.27, 4.2) * mm, v(-7.23, 4.19) * mm]});
            skFitSpline(sketch, "E106", {"points": [v(-7.23, 4.11) * mm, v(-7.22, 4.12) * mm, v(-7.2, 4.12) * mm, v(-7.17, 4.12) * mm, v(-7.11, 4.16) * mm, v(-7.04, 4.25) * mm, v(-6.9, 4.2) * mm, v(-6.8, 4.26) * mm, v(-6.73, 4.22) * mm, v(-6.7, 4.2) * mm, v(-6.66, 4.12) * mm, v(-6.64, 4.15) * mm, v(-6.63, 4.16) * mm, v(-6.61, 4.18) * mm, v(-6.57, 4.14) * mm, v(-6.53, 4.12) * mm, v(-6.43, 4.12) * mm, v(-6.3, 4.19) * mm, v(-6.13, 4.24) * mm, v(-5.98, 4.3) * mm, v(-5.86, 4.31) * mm, v(-5.76, 4.3) * mm, v(-5.63, 4.29) * mm, v(-5.47, 4.26) * mm, v(-5.27, 4.22) * mm, v(-5.07, 4.18) * mm, v(-4.86, 4.11) * mm, v(-4.7, 3.96) * mm, v(-4.6, 3.8) * mm, v(-4.54, 3.7) * mm, v(-4.49, 3.62) * mm, v(-4.44, 3.54) * mm, v(-4.4, 3.45) * mm, v(-4.35, 3.35) * mm, v(-4.31, 3.26) * mm, v(-4.27, 3.17) * mm, v(-4.23, 3.1) * mm, v(-4.2, 3.03) * mm, v(-4.2, 3) * mm]});
            skFitSpline(sketch, "E107", {"points": [v(-4.2, 3) * mm, v(-4.2, 3) * mm, v(-4.22, 2.98) * mm, v(-4.24, 2.96) * mm, v(-4.28, 2.94) * mm, v(-4.28, 2.93) * mm, v(-4.28, 2.92) * mm, v(-4.26, 2.87) * mm, v(-4.16, 2.81) * mm, v(-4.18, 2.66) * mm, v(-4.14, 2.48) * mm, v(-4.05, 2.29) * mm, v(-3.97, 2.05) * mm, v(-3.91, 1.86) * mm, v(-3.85, 1.73) * mm, v(-3.8, 1.65) * mm, v(-3.7, 1.55) * mm, v(-3.57, 1.4) * mm, v(-3.5, 1.18) * mm, v(-3.48, 0.96) * mm, v(-3.5, 0.72) * mm, v(-3.63, 0.54) * mm, v(-3.75, 0.44) * mm, v(-3.82, 0.37) * mm, v(-3.85, 0.34) * mm, v(-3.87, 0.33) * mm, v(-3.88, 0.32) * mm]});
            skFitSpline(sketch, "E108", {"points": [v(-3.88, 0.32) * mm, v(-3.97, 0.34) * mm, v(-4.16, 0.37) * mm, v(-4.45, 0.41) * mm, v(-4.74, 0.47) * mm, v(-5.05, 0.52) * mm, v(-5.37, 0.6) * mm, v(-5.64, 0.64) * mm, v(-5.86, 0.72) * mm, v(-6.03, 0.81) * mm, v(-6.17, 0.8) * mm, v(-6.26, 0.8) * mm, v(-6.3, 0.84) * mm, v(-6.34, 0.84) * mm, v(-6.36, 0.84) * mm]});
            skFitSpline(sketch, "E109", {"points": [v(-6.36, 0.84) * mm, v(-6.38, 0.85) * mm, v(-6.42, 0.86) * mm, v(-6.47, 0.87) * mm, v(-6.53, 0.89) * mm, v(-6.6, 0.9) * mm, v(-6.68, 0.93) * mm, v(-6.73, 0.94) * mm, v(-6.75, 0.95) * mm]});
            skFitSpline(sketch, "E110", {"points": [v(-6.75, 0.95) * mm, v(-6.76, 0.94) * mm, v(-6.76, 0.91) * mm, v(-6.76, 0.88) * mm, v(-6.77, 0.86) * mm, v(-6.77, 0.85) * mm]});
            skFitSpline(sketch, "E111", {"points": [v(-6.77, 0.85) * mm, v(-6.79, 0.86) * mm, v(-6.82, 0.89) * mm, v(-6.87, 0.92) * mm, v(-6.93, 0.94) * mm, v(-7, 0.92) * mm, v(-7.05, 0.9) * mm, v(-7.1, 0.87) * mm, v(-7.12, 0.86) * mm]});
            skFitSpline(sketch, "E112", {"points": [v(-7.12, 0.86) * mm, v(-7.12, 0.87) * mm, v(-7.13, 0.9) * mm, v(-7.14, 0.94) * mm, v(-7.14, 0.97) * mm, v(-7.15, 0.98) * mm]});
            skFitSpline(sketch, "E113", {"points": [v(-7.73, 0.98) * mm, v(-7.73, 0.97) * mm, v(-7.72, 0.94) * mm, v(-7.71, 0.9) * mm, v(-7.71, 0.87) * mm, v(-7.7, 0.86) * mm]});
            skFitSpline(sketch, "E114", {"points": [v(-7.7, 0.86) * mm, v(-7.76, 0.88) * mm, v(-7.86, 0.92) * mm, v(-8, 0.97) * mm, v(-8.1, 1) * mm, v(-8.16, 1.03) * mm]});
            skFitSpline(sketch, "E115", {"points": [v(-8.16, 1.03) * mm, v(-8.19, 1) * mm, v(-8.25, 0.95) * mm, v(-8.4, 0.97) * mm, v(-8.48, 1.02) * mm, v(-8.52, 1.05) * mm]});
            skFitSpline(sketch, "E116", {"points": [v(-8.52, 1.05) * mm, v(-8.52, 1.04) * mm, v(-8.53, 1.02) * mm, v(-8.53, 1) * mm, v(-8.53, 0.98) * mm, v(-8.53, 0.97) * mm]});
            skFitSpline(sketch, "E117", {"points": [v(-8.53, 0.97) * mm, v(-8.61, 0.99) * mm, v(-8.78, 1.02) * mm, v(-9.04, 0.97) * mm, v(-9.2, 1.05) * mm, v(-9.27, 1.09) * mm]});
            skFitSpline(sketch, "E118", {"points": [v(-9.27, 1.09) * mm, v(-9.29, 1.08) * mm, v(-9.32, 1.07) * mm, v(-9.36, 1.05) * mm, v(-9.47, 1.05) * mm, v(-9.63, 1.12) * mm, v(-9.86, 1.18) * mm, v(-10.12, 1.2) * mm, v(-10.38, 1.22) * mm, v(-10.66, 1.3) * mm, v(-10.95, 1.36) * mm, v(-11.27, 1.46) * mm, v(-11.6, 1.62) * mm, v(-11.85, 1.8) * mm, v(-12.1, 1.9) * mm, v(-12.3, 1.95) * mm, v(-12.6, 1.97) * mm, v(-12.96, 1.96) * mm, v(-13.4, 1.93) * mm, v(-13.74, 1.93) * mm, v(-13.99, 1.9) * mm, v(-14.12, 1.81) * mm, v(-14.24, 1.65) * mm, v(-14.38, 1.45) * mm, v(-14.6, 1.25) * mm, v(-14.92, 1.1) * mm, v(-15.28, 0.88) * mm, v(-15.59, 0.51) * mm, v(-15.8, 0.28) * mm, v(-15.9, 0.14) * mm, v(-15.92, 0.12) * mm, v(-16, 0.04) * mm, v(-16.14, -0.1) * mm, v(-16.25, -0.36) * mm, v(-16.31, -0.64) * mm, v(-16.39, -0.95) * mm, v(-16.47, -1.25) * mm, v(-16.53, -1.49) * mm, v(-16.57, -1.65) * mm, v(-16.6, -1.73) * mm, v(-16.7, -1.95) * mm, v(-16.87, -2.31) * mm, v(-17.02, -2.84) * mm, v(-17.13, -3.25) * mm, v(-17.22, -3.52) * mm, v(-17.27, -3.68) * mm, v(-17.36, -3.9) * mm, v(-17.43, -4.2) * mm, v(-17.43, -4.58) * mm, v(-17.42, -5) * mm, v(-17.47, -5.47) * mm, v(-17.54, -5.97) * mm, v(-17.72, -6.37) * mm, v(-17.84, -6.71) * mm, v(-17.85, -7.01) * mm, v(-17.84, -7.33) * mm, v(-17.84, -7.7) * mm, v(-17.85, -8.08) * mm, v(-17.83, -8.35) * mm, v(-17.85, -8.48) * mm, v(-17.85, -8.5) * mm, v(-17.84, -8.59) * mm, v(-17.8, -8.75) * mm, v(-17.88, -8.98) * mm, v(-17.96, -9.2) * mm, v(-18.01, -9.42) * mm, v(-18.07, -9.66) * mm, v(-18.14, -9.91) * mm, v(-18.25, -10.2) * mm, v(-18.37, -10.5) * mm, v(-18.48, -10.79) * mm, v(-18.59, -11.05) * mm, v(-18.68, -11.28) * mm, v(-18.77, -11.46) * mm, v(-18.8, -11.6) * mm, v(-18.79, -11.68) * mm, v(-18.79, -11.77) * mm, v(-18.8, -11.87) * mm, v(-18.82, -11.96) * mm, v(-18.86, -12.1) * mm, v(-18.93, -12.29) * mm, v(-19, -12.52) * mm, v(-19.07, -12.71) * mm, v(-19.13, -12.87) * mm, v(-19.19, -12.98) * mm, v(-19.23, -13.12) * mm, v(-19.26, -13.26) * mm, v(-19.27, -13.42) * mm, v(-19.29, -13.52) * mm, v(-19.3, -13.58) * mm]});
            skFitSpline(sketch, "E119", {"points": [v(-19.3, -13.58) * mm, v(-19.24, -13.59) * mm, v(-19.14, -13.6) * mm, v(-19.01, -13.54) * mm, v(-18.91, -13.43) * mm, v(-18.79, -13.3) * mm, v(-18.63, -13.17) * mm, v(-18.48, -13.02) * mm, v(-18.35, -12.85) * mm, v(-18.28, -12.65) * mm, v(-18.2, -12.44) * mm, v(-18.12, -12.22) * mm, v(-18.01, -12) * mm, v(-17.9, -11.78) * mm, v(-17.8, -11.58) * mm, v(-17.74, -11.38) * mm, v(-17.71, -11.14) * mm, v(-17.7, -10.88) * mm, v(-17.65, -10.6) * mm, v(-17.61, -10.3) * mm, v(-17.52, -10) * mm, v(-17.33, -9.75) * mm, v(-17.16, -9.54) * mm, v(-17.02, -9.37) * mm, v(-16.92, -9.25) * mm, v(-16.84, -9.17) * mm, v(-16.8, -9.1) * mm, v(-16.8, -9.06) * mm, v(-16.78, -8.98) * mm, v(-16.73, -8.86) * mm, v(-16.67, -8.7) * mm, v(-16.63, -8.57) * mm, v(-16.58, -8.47) * mm, v(-16.54, -8.4) * mm, v(-16.44, -8.16) * mm, v(-16.3, -7.72) * mm, v(-16.08, -7.12) * mm, v(-15.9, -6.6) * mm, v(-15.74, -6.15) * mm, v(-15.6, -5.79) * mm, v(-15.51, -5.52) * mm, v(-15.44, -5.36) * mm, v(-15.4, -5.3) * mm, v(-15.31, -5.19) * mm, v(-15.18, -5) * mm, v(-15, -4.74) * mm, v(-14.88, -4.58) * mm, v(-14.82, -4.5) * mm]});
            skFitSpline(sketch, "E120", {"points": [v(-14.82, -4.5) * mm, v(-14.83, -4.47) * mm, v(-14.85, -4.44) * mm, v(-14.88, -4.38) * mm, v(-14.9, -4.35) * mm, v(-14.9, -4.34) * mm]});
            skFitSpline(sketch, "E121", {"points": [v(-14.9, -4.34) * mm, v(-14.88, -4.33) * mm, v(-14.85, -4.32) * mm, v(-14.8, -4.3) * mm, v(-14.76, -4.3) * mm, v(-14.74, -4.29) * mm]});
            skFitSpline(sketch, "E122", {"points": [v(-14.74, -4.29) * mm, v(-14.72, -4.25) * mm, v(-14.68, -4.16) * mm, v(-14.63, -4.01) * mm, v(-14.59, -3.91) * mm, v(-14.56, -3.86) * mm]});
            skFitSpline(sketch, "E123", {"points": [v(-14.56, -3.86) * mm, v(-14.55, -3.84) * mm, v(-14.53, -3.8) * mm, v(-14.49, -3.75) * mm, v(-14.43, -3.67) * mm, v(-14.37, -3.58) * mm, v(-14.3, -3.48) * mm, v(-14.21, -3.37) * mm, v(-14.12, -3.26) * mm, v(-14.02, -3.14) * mm, v(-13.92, -3.01) * mm, v(-13.83, -2.87) * mm, v(-13.73, -2.72) * mm, v(-13.62, -2.55) * mm, v(-13.5, -2.37) * mm, v(-13.4, -2.16) * mm, v(-13.37, -1.95) * mm, v(-13.33, -1.78) * mm, v(-13.26, -1.65) * mm, v(-13.16, -1.53) * mm, v(-13.05, -1.4) * mm, v(-12.91, -1.3) * mm, v(-12.8, -1.18) * mm, v(-12.7, -1.1) * mm, v(-12.58, -1.09) * mm, v(-12.46, -1.11) * mm, v(-12.34, -1.18) * mm, v(-12.3, -1.36) * mm, v(-12.37, -1.54) * mm, v(-12.46, -1.75) * mm, v(-12.53, -1.99) * mm, v(-12.59, -2.22) * mm, v(-12.61, -2.44) * mm, v(-12.61, -2.64) * mm, v(-12.61, -2.88) * mm, v(-12.63, -3.13) * mm, v(-12.65, -3.41) * mm, v(-12.66, -3.67) * mm, v(-12.64, -3.92) * mm, v(-12.61, -4.14) * mm, v(-12.56, -4.45) * mm, v(-12.5, -4.82) * mm, v(-12.4, -5.28) * mm, v(-12.32, -5.72) * mm, v(-12.22, -6.14) * mm, v(-12.08, -6.53) * mm, v(-11.9, -6.9) * mm, v(-11.77, -7.25) * mm, v(-11.77, -7.63) * mm, v(-11.96, -7.99) * mm, v(-12.24, -8.32) * mm, v(-12.52, -8.7) * mm, v(-12.77, -9) * mm, v(-13, -9.21) * mm, v(-13.19, -9.35) * mm, v(-13.42, -9.5) * mm, v(-13.65, -9.7) * mm, v(-13.86, -9.97) * mm, v(-13.98, -10.23) * mm, v(-14.09, -10.45) * mm, v(-14.16, -10.64) * mm, v(-14.13, -10.82) * mm, v(-14.07, -10.94) * mm, v(-14.04, -11.04) * mm, v(-14, -11.2) * mm, v(-13.97, -11.44) * mm, v(-13.93, -11.74) * mm, v(-13.88, -12.03) * mm, v(-13.85, -12.3) * mm, v(-13.83, -12.56) * mm, v(-13.8, -12.82) * mm, v(-13.75, -13.08) * mm, v(-13.7, -13.35) * mm, v(-13.64, -13.64) * mm, v(-13.57, -13.94) * mm, v(-13.5, -14.25) * mm, v(-13.44, -14.57) * mm, v(-13.36, -14.88) * mm, v(-13.23, -15.17) * mm, v(-13.1, -15.43) * mm, v(-12.97, -15.66) * mm, v(-12.84, -15.86) * mm, v(-12.79, -16.06) * mm, v(-12.72, -16.23) * mm, v(-12.6, -16.33) * mm, v(-12.57, -16.43) * mm, v(-12.56, -16.48) * mm]});
            skFitSpline(sketch, "E124", {"points": [v(-5.18, -9.54) * mm, v(-5.18, -9.53) * mm, v(-5.16, -9.51) * mm, v(-5.14, -9.49) * mm, v(-5.14, -9.42) * mm, v(-5.21, -9.35) * mm, v(-5.27, -9.24) * mm, v(-5.31, -9.16) * mm, v(-5.33, -9.13) * mm]});
            skFitSpline(sketch, "E125", {"points": [v(-5.33, -9.13) * mm, v(-5.4, -9.16) * mm, v(-5.5, -9.22) * mm, v(-5.58, -9.36) * mm, v(-5.57, -9.45) * mm, v(-5.57, -9.5) * mm]});
            skFitSpline(sketch, "E126", {"points": [v(-5.57, -9.5) * mm, v(-5.6, -9.54) * mm, v(-5.66, -9.62) * mm, v(-5.74, -9.74) * mm, v(-5.8, -9.8) * mm, v(-5.82, -9.84) * mm]});
            skFitSpline(sketch, "E127", {"points": [v(-5.82, -9.84) * mm, v(-5.81, -9.88) * mm, v(-5.8, -9.95) * mm, v(-5.8, -10.05) * mm, v(-5.79, -10.14) * mm, v(-5.8, -10.23) * mm, v(-5.81, -10.32) * mm, v(-5.83, -10.45) * mm, v(-5.83, -10.62) * mm, v(-5.83, -10.83) * mm, v(-5.83, -11.03) * mm, v(-5.86, -11.22) * mm, v(-5.89, -11.4) * mm, v(-5.9, -11.58) * mm, v(-5.91, -11.76) * mm, v(-5.91, -11.95) * mm, v(-5.9, -12.2) * mm, v(-5.91, -12.53) * mm, v(-5.9, -12.93) * mm, v(-5.79, -13.25) * mm, v(-5.66, -13.5) * mm, v(-5.57, -13.68) * mm, v(-5.5, -13.91) * mm, v(-5.44, -14.17) * mm, v(-5.3, -14.42) * mm, v(-5.16, -14.64) * mm, v(-5, -14.82) * mm, v(-4.87, -14.97) * mm, v(-4.76, -15.1) * mm, v(-4.67, -15.2) * mm, v(-4.6, -15.28) * mm, v(-4.48, -15.37) * mm, v(-4.3, -15.48) * mm, v(-4.09, -15.6) * mm, v(-3.84, -15.74) * mm, v(-3.57, -15.87) * mm, v(-3.28, -15.98) * mm, v(-3.08, -16.11) * mm, v(-2.92, -16.15) * mm, v(-2.83, -16.14) * mm, v(-2.74, -16.24) * mm, v(-2.64, -16.35) * mm, v(-2.48, -16.46) * mm, v(-2.29, -16.57) * mm, v(-2.07, -16.72) * mm, v(-1.88, -16.93) * mm, v(-1.74, -17.15) * mm, v(-1.63, -17.35) * mm, v(-1.57, -17.55) * mm, v(-1.6, -17.72) * mm, v(-1.65, -17.84) * mm, v(-1.65, -17.96) * mm, v(-1.57, -18.02) * mm, v(-1.52, -18.08) * mm, v(-1.51, -18.14) * mm, v(-1.48, -18.24) * mm, v(-1.5, -18.4) * mm, v(-1.63, -18.55) * mm, v(-1.83, -18.59) * mm, v(-2.03, -18.55) * mm, v(-2.23, -18.52) * mm, v(-2.4, -18.5) * mm, v(-2.51, -18.47) * mm, v(-2.58, -18.44) * mm, v(-2.66, -18.42) * mm, v(-2.75, -18.4) * mm, v(-2.84, -18.37) * mm, v(-2.98, -18.35) * mm, v(-3.18, -18.35) * mm, v(-3.42, -18.34) * mm, v(-3.65, -18.33) * mm, v(-3.88, -18.29) * mm, v(-4.1, -18.24) * mm, v(-4.34, -18.2) * mm, v(-4.6, -18.16) * mm, v(-4.9, -18.14) * mm, v(-5.16, -18.1) * mm, v(-5.39, -18.07) * mm, v(-5.58, -18.03) * mm, v(-5.83, -17.98) * mm, v(-6.12, -17.9) * mm, v(-6.4, -17.7) * mm, v(-6.62, -17.55) * mm, v(-6.73, -17.38) * mm, v(-6.72, -17.27) * mm, v(-6.79, -17.2) * mm, v(-6.84, -17.15) * mm, v(-6.87, -17.1) * mm, v(-6.91, -17.04) * mm, v(-6.99, -17) * mm, v(-7.07, -16.96) * mm, v(-7.18, -16.9) * mm, v(-7.3, -16.83) * mm, v(-7.46, -16.74) * mm, v(-7.65, -16.65) * mm, v(-7.88, -16.55) * mm, v(-8.15, -16.44) * mm, v(-8.4, -16.32) * mm, v(-8.63, -16.18) * mm, v(-8.83, -16.03) * mm, v(-9, -15.9) * mm, v(-9.1, -15.78) * mm, v(-9.17, -15.68) * mm, v(-9.22, -15.55) * mm, v(-9.3, -15.43) * mm, v(-9.38, -15.33) * mm, v(-9.46, -15.3) * mm, v(-9.5, -15.3) * mm]});
            skFitSpline(sketch, "E128", {"points": [v(-9.5, -15.3) * mm, v(-9.5, -15.28) * mm, v(-9.49, -15.25) * mm, v(-9.48, -15.2) * mm, v(-9.5, -15.13) * mm, v(-9.6, -15.07) * mm, v(-9.67, -14.94) * mm, v(-9.75, -14.8) * mm, v(-9.81, -14.68) * mm, v(-9.9, -14.56) * mm, v(-10, -14.51) * mm, v(-10.08, -14.45) * mm, v(-10.1, -14.38) * mm, v(-10.12, -14.33) * mm, v(-10.13, -14.31) * mm]});
            skFitSpline(sketch, "E129", {"points": [v(-10.13, -14.31) * mm, v(-10.14, -14.3) * mm, v(-10.17, -14.3) * mm, v(-10.22, -14.28) * mm, v(-10.25, -14.27) * mm, v(-10.27, -14.26) * mm]});
            skFitSpline(sketch, "E130", {"points": [v(-10.27, -14.26) * mm, v(-10.24, -14.23) * mm, v(-10.19, -14.16) * mm, v(-10.18, -14.03) * mm, v(-10.24, -13.91) * mm, v(-10.32, -13.8) * mm, v(-10.39, -13.68) * mm, v(-10.47, -13.57) * mm, v(-10.5, -13.43) * mm, v(-10.46, -13.3) * mm, v(-10.45, -13.1) * mm, v(-10.46, -12.85) * mm, v(-10.32, -12.57) * mm, v(-10.17, -12.37) * mm, v(-10.03, -12.22) * mm, v(-9.93, -12.09) * mm, v(-9.87, -11.93) * mm, v(-9.82, -11.78) * mm, v(-9.73, -11.65) * mm, v(-9.54, -11.49) * mm, v(-9.24, -11.32) * mm, v(-8.88, -11.06) * mm, v(-8.63, -10.8) * mm, v(-8.45, -10.62) * mm, v(-8.33, -10.5) * mm, v(-8.2, -10.4) * mm, v(-8.08, -10.29) * mm, v(-7.95, -10.2) * mm, v(-7.83, -10.1) * mm, v(-7.7, -10.01) * mm, v(-7.58, -9.94) * mm, v(-7.46, -9.83) * mm, v(-7.37, -9.69) * mm, v(-7.29, -9.52) * mm, v(-7.2, -9.37) * mm, v(-7.12, -9.24) * mm, v(-7.04, -9.12) * mm, v(-6.95, -9.02) * mm, v(-6.82, -8.97) * mm, v(-6.7, -8.94) * mm, v(-6.63, -8.86) * mm, v(-6.58, -8.81) * mm, v(-6.55, -8.8) * mm, v(-6.5, -8.75) * mm, v(-6.46, -8.65) * mm, v(-6.33, -8.58) * mm, v(-6.25, -8.6) * mm, v(-6.2, -8.6) * mm]});
            skFitSpline(sketch, "E131", {"points": [v(-6.2, -8.6) * mm, v(-6.17, -8.55) * mm, v(-6.1, -8.46) * mm, v(-6, -8.32) * mm, v(-5.85, -8.14) * mm, v(-5.65, -7.93) * mm, v(-5.38, -7.7) * mm, v(-5.14, -7.56) * mm, v(-4.97, -7.45) * mm, v(-4.85, -7.38) * mm, v(-4.74, -7.4) * mm, v(-4.67, -7.4) * mm, v(-4.63, -7.38) * mm, v(-4.55, -7.32) * mm, v(-4.44, -7.21) * mm, v(-4.27, -7.1) * mm, v(-4, -7.03) * mm, v(-3.67, -7.01) * mm, v(-3.27, -7.1) * mm, v(-3.07, -7.33) * mm, v(-2.94, -7.47) * mm, v(-2.87, -7.52) * mm, v(-2.78, -7.56) * mm, v(-2.7, -7.6) * mm, v(-2.64, -7.7) * mm, v(-2.64, -7.8) * mm, v(-2.65, -7.91) * mm, v(-2.64, -8.02) * mm, v(-2.63, -8.14) * mm, v(-2.6, -8.25) * mm, v(-2.57, -8.36) * mm, v(-2.53, -8.53) * mm, v(-2.49, -8.74) * mm, v(-2.43, -9.02) * mm, v(-2.39, -9.24) * mm, v(-2.35, -9.42) * mm, v(-2.32, -9.56) * mm, v(-2.33, -9.71) * mm, v(-2.33, -9.87) * mm, v(-2.28, -10.04) * mm, v(-2.3, -10.15) * mm, v(-2.32, -10.22) * mm, v(-2.3, -10.24) * mm, v(-2.29, -10.28) * mm, v(-2.24, -10.33) * mm, v(-2.3, -10.4) * mm, v(-2.34, -10.4) * mm, v(-2.36, -10.4) * mm]});
            skFitSpline(sketch, "E132", {"points": [v(-2.36, -10.4) * mm, v(-2.35, -10.47) * mm, v(-2.34, -10.62) * mm, v(-2.31, -10.84) * mm, v(-2.29, -11.02) * mm, v(-2.29, -11.17) * mm, v(-2.3, -11.29) * mm, v(-2.3, -11.44) * mm, v(-2.22, -11.62) * mm, v(-2.05, -11.75) * mm, v(-1.9, -11.88) * mm, v(-1.78, -12.01) * mm, v(-1.65, -12.12) * mm, v(-1.56, -12.2) * mm, v(-1.51, -12.23) * mm]});
            skFitSpline(sketch, "E133", {"points": [v(-1.51, -12.23) * mm, v(-1.51, -12.23) * mm, v(-1.5, -12.23) * mm, v(-1.49, -12.24) * mm, v(-1.43, -12.26) * mm, v(-1.36, -12.32) * mm, v(-1.3, -12.42) * mm, v(-1.2, -12.54) * mm, v(-1.05, -12.65) * mm, v(-0.87, -12.77) * mm, v(-0.68, -12.85) * mm, v(-0.51, -12.95) * mm, v(-0.36, -13.06) * mm, v(-0.21, -13.07) * mm, v(-0.11, -13.07) * mm, v(-0.06, -13.1) * mm, v(-0.03, -13.1) * mm, v(0, -13.1) * mm]});
            skFitSpline(sketch, "E134", {"points": [v(0, -13.1) * mm, v(0, -13.12) * mm, v(-0.01, -13.14) * mm, v(-0.02, -13.16) * mm, v(-0.03, -13.2) * mm, v(-0.01, -13.19) * mm, v(0, -13.18) * mm, v(0.02, -13.16) * mm, v(0.04, -13.22) * mm, v(0.07, -13.25) * mm, v(0.09, -13.27) * mm, v(0.1, -13.28) * mm]});
            skFitSpline(sketch, "E135", {"points": [v(0.1, -13.28) * mm, v(0.12, -13.28) * mm, v(0.18, -13.28) * mm, v(0.25, -13.28) * mm, v(0.34, -13.3) * mm, v(0.42, -13.31) * mm, v(0.52, -13.25) * mm, v(0.56, -13.16) * mm, v(0.59, -13.05) * mm, v(0.57, -12.93) * mm, v(0.53, -12.86) * mm, v(0.5, -12.78) * mm, v(0.49, -12.73) * mm, v(0.5, -12.66) * mm, v(0.46, -12.67) * mm, v(0.44, -12.67) * mm, v(0.39, -12.65) * mm, v(0.32, -12.6) * mm, v(0.23, -12.53) * mm, v(0.13, -12.5) * mm, v(0.12, -12.42) * mm, v(0.13, -12.38) * mm, v(0.15, -12.34) * mm, v(0.14, -12.32) * mm, v(0.12, -12.31) * mm, v(0.1, -12.29) * mm, v(0.07, -12.25) * mm, v(0.02, -12.2) * mm, v(0, -12.15) * mm, v(-0.02, -12.13) * mm]});
            skFitSpline(sketch, "E136", {"points": [v(-0.02, -12.13) * mm, v(-0.04, -12.14) * mm, v(-0.08, -12.16) * mm, v(-0.15, -12.18) * mm, v(-0.2, -12.2) * mm, v(-0.21, -12.21) * mm]});
            skFitSpline(sketch, "E137", {"points": [v(-0.21, -12.21) * mm, v(-0.22, -12.19) * mm, v(-0.24, -12.14) * mm, v(-0.26, -12.06) * mm, v(-0.28, -12) * mm, v(-0.3, -11.98) * mm]});
            skFitSpline(sketch, "E138", {"points": [v(-0.3, -11.98) * mm, v(-0.28, -11.98) * mm, v(-0.26, -11.97) * mm, v(-0.23, -11.97) * mm, v(-0.19, -11.97) * mm, v(-0.22, -11.93) * mm, v(-0.23, -11.9) * mm, v(-0.27, -11.86) * mm, v(-0.35, -11.82) * mm, v(-0.46, -11.75) * mm, v(-0.53, -11.7) * mm, v(-0.56, -11.69) * mm]});
            skFitSpline(sketch, "E139", {"points": [v(-0.56, -11.69) * mm, v(-0.56, -11.66) * mm, v(-0.54, -11.6) * mm, v(-0.52, -11.52) * mm, v(-0.5, -11.46) * mm, v(-0.5, -11.43) * mm]});
            skFitSpline(sketch, "E140", {"points": [v(-0.5, -11.43) * mm, v(-0.53, -11.46) * mm, v(-0.59, -11.51) * mm, v(-0.67, -11.44) * mm, v(-0.66, -11.39) * mm, v(-0.66, -11.35) * mm]});
            skFitSpline(sketch, "E141", {"points": [v(-0.66, -11.35) * mm, v(-0.67, -11.36) * mm, v(-0.7, -11.38) * mm, v(-0.76, -11.41) * mm, v(-0.8, -11.43) * mm, v(-0.82, -11.45) * mm]});
            skFitSpline(sketch, "E142", {"points": [v(-0.82, -11.45) * mm, v(-0.83, -11.41) * mm, v(-0.86, -11.35) * mm, v(-0.92, -11.26) * mm, v(-0.93, -11.15) * mm, v(-0.98, -11.15) * mm, v(-1, -11.15) * mm, v(-1.01, -11.14) * mm, v(-1.02, -11.14) * mm]});
            skFitSpline(sketch, "E143", {"points": [v(-1.02, -11.14) * mm, v(-1.02, -11.12) * mm, v(-1, -11.07) * mm, v(-1, -11) * mm, v(-0.98, -10.95) * mm, v(-0.98, -10.92) * mm]});
            skFitSpline(sketch, "E144", {"points": [v(-0.98, -10.92) * mm, v(-1, -10.94) * mm, v(-1.04, -10.97) * mm, v(-1.12, -10.95) * mm, v(-1.13, -10.88) * mm, v(-1.12, -10.83) * mm, v(-1.14, -10.8) * mm, v(-1.19, -10.78) * mm, v(-1.23, -10.71) * mm, v(-1.23, -10.62) * mm, v(-1.19, -10.58) * mm, v(-1.17, -10.57) * mm]});
            skFitSpline(sketch, "E145", {"points": [v(-1.17, -10.57) * mm, v(-1.17, -10.54) * mm, v(-1.17, -10.48) * mm, v(-1.17, -10.4) * mm, v(-1.18, -10.29) * mm, v(-1.17, -10.16) * mm, v(-1.16, -9.99) * mm, v(-1.25, -9.9) * mm, v(-1.29, -9.86) * mm, v(-1.29, -9.85) * mm, v(-1.28, -9.8) * mm, v(-1.27, -9.69) * mm, v(-1.26, -9.54) * mm, v(-1.25, -9.43) * mm, v(-1.25, -9.36) * mm, v(-1.24, -9.33) * mm, v(-1.27, -9.28) * mm, v(-1.3, -9.19) * mm, v(-1.24, -9.06) * mm, v(-1.3, -8.99) * mm, v(-1.33, -8.95) * mm]});
            skFitSpline(sketch, "E146", {"points": [v(-1.33, -8.95) * mm, v(-1.33, -8.95) * mm, v(-1.32, -8.94) * mm, v(-1.3, -8.93) * mm, v(-1.28, -8.88) * mm, v(-1.26, -8.8) * mm, v(-1.2, -8.67) * mm, v(-1.19, -8.54) * mm, v(-1.1, -8.4) * mm, v(-1, -8.29) * mm, v(-0.85, -8.23) * mm, v(-0.75, -8.3) * mm, v(-0.66, -8.35) * mm, v(-0.58, -8.4) * mm, v(-0.48, -8.46) * mm, v(-0.4, -8.48) * mm, v(-0.31, -8.57) * mm, v(-0.28, -8.54) * mm, v(-0.27, -8.53) * mm, v(-0.26, -8.51) * mm, v(-0.26, -8.5) * mm]});
            skFitSpline(sketch, "E147", {"points": [v(-0.26, -8.5) * mm, v(-0.2, -8.58) * mm, v(-0.1, -8.7) * mm, v(0.12, -8.8) * mm, v(0.26, -8.75) * mm, v(0.33, -8.73) * mm]});
            skFitSpline(sketch, "E148", {"points": [v(0.33, -8.73) * mm, v(0.35, -8.8) * mm, v(0.4, -8.94) * mm, v(0.52, -9.14) * mm, v(0.46, -9.3) * mm, v(0.47, -9.38) * mm, v(0.48, -9.39) * mm, v(0.5, -9.45) * mm, v(0.56, -9.54) * mm, v(0.63, -9.7) * mm, v(0.58, -9.82) * mm, v(0.56, -9.88) * mm, v(0.57, -9.9) * mm, v(0.57, -9.94) * mm, v(0.59, -10) * mm, v(0.6, -10.1) * mm, v(0.63, -10.22) * mm, v(0.66, -10.34) * mm, v(0.7, -10.48) * mm, v(0.7, -10.59) * mm, v(0.74, -10.65) * mm, v(0.76, -10.68) * mm, v(0.77, -10.72) * mm, v(0.74, -10.78) * mm, v(0.77, -10.85) * mm, v(0.8, -10.9) * mm, v(0.83, -10.98) * mm, v(0.8, -11.05) * mm, v(0.83, -11.12) * mm, v(0.8, -11.14) * mm, v(0.8, -11.14) * mm, v(0.77, -11.15) * mm, v(0.84, -11.2) * mm, v(0.86, -11.23) * mm, v(0.9, -11.27) * mm, v(0.91, -11.29) * mm]});
            skFitSpline(sketch, "E149", {"points": [v(0.91, -11.29) * mm, v(0.88, -11.3) * mm, v(0.82, -11.3) * mm, v(0.73, -11.3) * mm, v(0.67, -11.31) * mm, v(0.64, -11.32) * mm]});
            skFitSpline(sketch, "E150", {"points": [v(0.64, -11.32) * mm, v(0.64, -11.32) * mm, v(0.64, -11.33) * mm, v(0.64, -11.35) * mm, v(0.64, -11.37) * mm, v(0.64, -11.37) * mm]});
            skFitSpline(sketch, "E151", {"points": [v(0.64, -11.37) * mm, v(0.67, -11.37) * mm, v(0.73, -11.36) * mm, v(0.83, -11.39) * mm, v(0.83, -11.45) * mm, v(0.83, -11.5) * mm]});
            skFitSpline(sketch, "E152", {"points": [v(0.83, -11.5) * mm, v(0.82, -11.5) * mm, v(0.78, -11.5) * mm, v(0.76, -11.59) * mm, v(0.77, -11.64) * mm, v(0.77, -11.68) * mm]});
            skFitSpline(sketch, "E153", {"points": [v(0.77, -11.68) * mm, v(0.76, -11.69) * mm, v(0.74, -11.7) * mm, v(0.71, -11.72) * mm, v(0.7, -11.73) * mm, v(0.68, -11.74) * mm]});
            skFitSpline(sketch, "E154", {"points": [v(0.68, -11.74) * mm, v(0.7, -11.78) * mm, v(0.72, -11.86) * mm, v(0.77, -11.98) * mm, v(0.8, -12.06) * mm, v(0.8, -12.1) * mm]});
            skFitSpline(sketch, "E155", {"points": [v(0.8, -12.1) * mm, v(0.8, -12.1) * mm, v(0.8, -12.13) * mm, v(0.78, -12.15) * mm, v(0.76, -12.17) * mm, v(0.76, -12.18) * mm]});
            skFitSpline(sketch, "E156", {"points": [v(0.76, -12.18) * mm, v(0.77, -12.2) * mm, v(0.8, -12.22) * mm, v(0.84, -12.25) * mm, v(0.89, -12.31) * mm, v(0.81, -12.4) * mm, v(0.9, -12.5) * mm, v(0.96, -12.54) * mm, v(1, -12.58) * mm, v(1, -12.6) * mm, v(1.03, -12.65) * mm, v(1.06, -12.7) * mm, v(1.08, -12.8) * mm, v(1.14, -12.85) * mm, v(1.12, -12.9) * mm, v(1.11, -12.92) * mm, v(1.08, -12.95) * mm, v(1.1, -12.96) * mm, v(1.12, -12.96) * mm, v(1.14, -12.98) * mm, v(1.16, -12.93) * mm, v(1.2, -12.9) * mm, v(1.23, -12.86) * mm, v(1.24, -12.84) * mm]});
            skFitSpline(sketch, "E157", {"points": [v(1.24, -13.05) * mm, v(1.33, -13.04) * mm, v(1.49, -13.02) * mm, v(1.67, -13.2) * mm, v(1.82, -13.24) * mm, v(1.9, -13.26) * mm]});
            skFitSpline(sketch, "E158", {"points": [v(1.9, -13.26) * mm, v(1.92, -13.25) * mm, v(1.98, -13.23) * mm, v(2.06, -13.21) * mm, v(2.14, -13.21) * mm, v(2.22, -13.23) * mm, v(2.3, -13.28) * mm, v(2.36, -13.3) * mm, v(2.38, -13.33) * mm, v(2.38, -13.35) * mm, v(2.4, -13.38) * mm, v(2.44, -13.4) * mm, v(2.5, -13.44) * mm, v(2.53, -13.47) * mm, v(2.58, -13.46) * mm, v(2.6, -13.44) * mm, v(2.64, -13.43) * mm, v(2.67, -13.42) * mm, v(2.7, -13.4) * mm, v(2.75, -13.4) * mm, v(2.81, -13.44) * mm, v(2.9, -13.47) * mm, v(2.96, -13.5) * mm, v(3, -13.51) * mm]});
            skFitSpline(sketch, "E159", {"points": [v(3, -13.51) * mm, v(3, -13.5) * mm, v(3, -13.48) * mm, v(3.01, -13.46) * mm, v(3.04, -13.38) * mm, v(3.23, -13.5) * mm, v(3.4, -13.5) * mm, v(3.58, -13.53) * mm, v(3.76, -13.51) * mm, v(3.94, -13.47) * mm, v(4.05, -13.44) * mm, v(4.11, -13.43) * mm]});
            skFitSpline(sketch, "E160", {"points": [v(4.11, -13.43) * mm, v(4.12, -13.39) * mm, v(4.15, -13.3) * mm, v(4.1, -13.19) * mm, v(4.03, -13.1) * mm, v(3.96, -13.05) * mm, v(3.9, -13) * mm, v(3.87, -12.93) * mm, v(3.83, -12.85) * mm, v(3.76, -12.8) * mm, v(3.63, -12.75) * mm, v(3.44, -12.7) * mm, v(3.22, -12.58) * mm, v(3.03, -12.47) * mm, v(2.87, -12.35) * mm, v(2.73, -12.23) * mm, v(2.55, -12.15) * mm, v(2.35, -12.05) * mm, v(2.26, -11.84) * mm, v(2.17, -11.7) * mm, v(2.1, -11.57) * mm, v(2.1, -11.46) * mm, v(2.1, -11.35) * mm, v(2.07, -11.25) * mm, v(2.03, -11.16) * mm, v(2.04, -11.06) * mm, v(2, -11.04) * mm, v(1.96, -11.02) * mm, v(1.94, -11.01) * mm, v(1.93, -11) * mm]});
            skFitSpline(sketch, "E161", {"points": [v(1.93, -11) * mm, v(1.94, -11) * mm, v(1.95, -10.97) * mm, v(1.97, -10.93) * mm, v(1.99, -10.86) * mm, v(1.97, -10.76) * mm, v(1.96, -10.63) * mm, v(1.95, -10.47) * mm, v(1.96, -10.3) * mm, v(2.04, -10.13) * mm, v(2.16, -10.08) * mm, v(2.22, -10.06) * mm]});
            skFitSpline(sketch, "E162", {"points": [v(2.22, -10.06) * mm, v(2.2, -10.03) * mm, v(2.17, -9.98) * mm, v(2.13, -9.87) * mm, v(2.23, -9.86) * mm, v(2.26, -9.82) * mm, v(2.27, -9.79) * mm, v(2.3, -9.7) * mm, v(2.35, -9.54) * mm, v(2.57, -9.46) * mm, v(2.75, -9.54) * mm, v(2.9, -9.61) * mm, v(3.03, -9.66) * mm, v(3.17, -9.73) * mm, v(3.33, -9.8) * mm, v(3.5, -9.89) * mm, v(3.64, -9.96) * mm, v(3.74, -10) * mm, v(3.8, -10) * mm, v(3.93, -10.02) * mm, v(4.14, -10.05) * mm, v(4.42, -10.1) * mm, v(4.75, -10.16) * mm, v(5.12, -10.25) * mm, v(5.54, -10.34) * mm, v(5.93, -10.35) * mm, v(6.28, -10.36) * mm, v(6.58, -10.4) * mm, v(6.87, -10.44) * mm, v(7.13, -10.5) * mm, v(7.38, -10.54) * mm, v(7.58, -10.59) * mm, v(7.72, -10.62) * mm, v(7.82, -10.64) * mm, v(7.94, -10.72) * mm, v(8.08, -10.85) * mm, v(8.3, -10.97) * mm, v(8.47, -11) * mm, v(8.56, -11.03) * mm, v(8.57, -11.04) * mm, v(8.64, -11.07) * mm, v(8.8, -11.13) * mm, v(9.01, -11.23) * mm, v(9.32, -11.3) * mm, v(9.69, -11.35) * mm, v(10.1, -11.54) * mm, v(10.36, -11.8) * mm, v(10.55, -12.02) * mm, v(10.71, -12.13) * mm, v(10.94, -12.23) * mm, v(11.22, -12.36) * mm, v(11.46, -12.66) * mm, v(11.53, -12.92) * mm, v(11.55, -13.1) * mm, v(11.56, -13.17) * mm, v(11.57, -13.36) * mm, v(11.6, -13.68) * mm, v(11.58, -14.12) * mm, v(11.44, -14.4) * mm, v(11.34, -14.55) * mm, v(11.32, -14.6) * mm, v(11.3, -14.7) * mm, v(11.3, -14.85) * mm, v(11.27, -15.07) * mm, v(11.28, -15.32) * mm, v(11.3, -15.6) * mm, v(11.28, -15.92) * mm, v(11.18, -16.22) * mm, v(11.04, -16.52) * mm, v(10.94, -16.83) * mm, v(10.9, -17.08) * mm, v(10.88, -17.25) * mm, v(10.85, -17.33) * mm, v(10.79, -17.45) * mm, v(10.71, -17.6) * mm, v(10.66, -17.8) * mm, v(10.67, -18.1) * mm, v(10.64, -18.46) * mm, v(10.35, -18.84) * mm, v(10.02, -18.92) * mm, v(9.83, -18.96) * mm, v(9.78, -18.98) * mm, v(9.65, -18.95) * mm, v(9.49, -18.84) * mm, v(9.22, -18.83) * mm, v(9.01, -18.87) * mm, v(8.86, -18.91) * mm, v(8.76, -18.93) * mm, v(8.6, -18.94) * mm, v(8.37, -18.92) * mm, v(8.08, -18.9) * mm, v(7.8, -18.88) * mm, v(7.53, -18.85) * mm, v(7.25, -18.83) * mm, v(7.08, -18.94) * mm, v(6.98, -18.99) * mm, v(6.94, -18.99) * mm, v(6.8, -19) * mm, v(6.57, -19.03) * mm, v(6.23, -18.98) * mm, v(5.86, -19) * mm, v(5.47, -19.04) * mm, v(5.06, -19.02) * mm, v(4.7, -19) * mm, v(4.38, -18.99) * mm, v(4.11, -18.96) * mm, v(3.89, -18.92) * mm, v(3.7, -18.89) * mm, v(3.54, -18.9) * mm, v(3.33, -18.97) * mm, v(3.06, -19.06) * mm, v(2.71, -19.07) * mm, v(2.4, -19) * mm, v(2.13, -18.93) * mm, v(1.87, -18.9) * mm, v(1.6, -18.83) * mm, v(1.34, -18.76) * mm, v(1.05, -18.75) * mm, v(0.8, -18.78) * mm, v(0.6, -18.8) * mm, v(0.44, -18.8) * mm, v(0.28, -18.79) * mm, v(0.13, -18.76) * mm, v(0, -18.72) * mm, v(-0.15, -18.65) * mm, v(-0.3, -18.53) * mm, v(-0.41, -18.34) * mm, v(-0.44, -18.07) * mm, v(-0.34, -17.75) * mm, v(-0.04, -17.48) * mm, v(0.35, -17.42) * mm, v(0.73, -17.4) * mm, v(1.11, -17.37) * mm, v(1.5, -17.35) * mm, v(1.89, -17.33) * mm, v(2.29, -17.33) * mm, v(2.67, -17.35) * mm, v(3.02, -17.4) * mm, v(3.35, -17.43) * mm, v(3.7, -17.4) * mm, v(4.02, -17.38) * mm, v(4.36, -17.37) * mm, v(4.73, -17.3) * mm, v(5.15, -17.16) * mm, v(5.63, -17.08) * mm, v(5.97, -17.08) * mm, v(6.17, -17.05) * mm, v(6.22, -17.03) * mm, v(6.35, -16.95) * mm, v(6.55, -16.82) * mm, v(6.83, -16.65) * mm, v(7.06, -16.48) * mm, v(7.3, -16.38) * mm, v(7.5, -16.34) * mm, v(7.68, -16.18) * mm, v(7.83, -16) * mm, v(8.01, -15.84) * mm, v(8.18, -15.6) * mm, v(8.3, -15.32) * mm, v(8.43, -14.99) * mm, v(8.55, -14.64) * mm, v(8.63, -14.25) * mm, v(8.59, -13.85) * mm, v(8.65, -13.57) * mm, v(8.6, -13.43) * mm, v(8.58, -13.42) * mm, v(8.58, -13.42) * mm, v(8.57, -13.41) * mm]});
            skFitSpline(sketch, "E163", {"points": [v(8.57, -13.41) * mm, v(8.48, -13.42) * mm, v(8.3, -13.43) * mm, v(8.05, -13.54) * mm, v(7.8, -13.66) * mm, v(7.56, -13.78) * mm, v(7.3, -13.88) * mm, v(7.01, -13.96) * mm, v(6.7, -14.02) * mm, v(6.34, -14.06) * mm, v(6.04, -14.1) * mm, v(5.77, -14.16) * mm, v(5.56, -14.2) * mm, v(5.39, -14.23) * mm, v(5.28, -14.27) * mm, v(5.23, -14.3) * mm, v(5.12, -14.33) * mm, v(4.95, -14.31) * mm, v(4.73, -14.32) * mm, v(4.5, -14.37) * mm, v(4.23, -14.42) * mm, v(3.94, -14.4) * mm, v(3.7, -14.4) * mm, v(3.53, -14.42) * mm, v(3.4, -14.43) * mm, v(3.23, -14.45) * mm, v(3, -14.48) * mm, v(2.74, -14.51) * mm, v(2.54, -14.54) * mm, v(2.41, -14.55) * mm, v(2.36, -14.56) * mm, v(2.3, -14.57) * mm, v(2.25, -14.58) * mm, v(2.19, -14.59) * mm, v(2.15, -14.6) * mm, v(2.13, -14.6) * mm]});
            skFitSpline(sketch, "E164", {"points": [v(2.13, -14.6) * mm, v(2.13, -14.6) * mm, v(2.14, -14.63) * mm, v(2.16, -14.67) * mm, v(2.17, -14.7) * mm, v(2.18, -14.72) * mm]});
            skFitSpline(sketch, "E165", {"points": [v(2.18, -14.72) * mm, v(2.14, -14.7) * mm, v(2.08, -14.68) * mm, v(1.98, -14.65) * mm, v(1.93, -14.63) * mm, v(1.9, -14.62) * mm]});
            skFitSpline(sketch, "E166", {"points": [v(1.9, -14.62) * mm, v(1.88, -14.64) * mm, v(1.82, -14.69) * mm, v(1.75, -14.76) * mm, v(1.54, -14.92) * mm, v(1.16, -15.1) * mm, v(0.62, -15.32) * mm, v(0.28, -15.55) * mm, v(0.06, -15.68) * mm, v(-0.03, -15.7) * mm, v(-0.1, -15.72) * mm, v(-0.16, -15.74) * mm, v(-0.2, -15.75) * mm, v(-0.26, -15.77) * mm, v(-0.31, -15.8) * mm, v(-0.37, -15.85) * mm, v(-0.36, -15.98) * mm, v(-0.33, -16.12) * mm, v(-0.4, -16.27) * mm, v(-0.5, -16.3) * mm, v(-0.54, -16.33) * mm]});
            skFitSpline(sketch, "E167", {"points": [v(-0.54, -16.33) * mm, v(-0.53, -16.34) * mm, v(-0.52, -16.37) * mm, v(-0.5, -16.4) * mm, v(-0.48, -16.43) * mm, v(-0.47, -16.44) * mm]});
            skFitSpline(sketch, "E168", {"points": [v(-0.47, -16.44) * mm, v(-0.48, -16.48) * mm, v(-0.5, -16.55) * mm, v(-0.53, -16.66) * mm, v(-0.55, -16.73) * mm, v(-0.56, -16.76) * mm]});
            skFitSpline(sketch, "E169", {"points": [v(-0.56, -16.76) * mm, v(-0.54, -16.77) * mm, v(-0.51, -16.79) * mm, v(-0.47, -16.82) * mm, v(-0.44, -16.84) * mm, v(-0.42, -16.85) * mm]});
            skFitSpline(sketch, "E170", {"points": [v(-0.42, -16.85) * mm, v(-0.45, -16.9) * mm, v(-0.5, -16.99) * mm, v(-0.6, -17.13) * mm, v(-0.65, -17.22) * mm, v(-0.68, -17.27) * mm]});
            skFitSpline(sketch, "E171", {"points": [v(-0.68, -17.27) * mm, v(-0.66, -17.27) * mm, v(-0.63, -17.28) * mm, v(-0.59, -17.3) * mm, v(-0.53, -17.3) * mm, v(-0.53, -17.34) * mm, v(-0.52, -17.36) * mm, v(-0.52, -17.37) * mm, v(-0.52, -17.38) * mm]});
            skFitSpline(sketch, "E172", {"points": [v(-0.52, -17.38) * mm, v(-0.55, -17.4) * mm, v(-0.6, -17.44) * mm, v(-0.7, -17.5) * mm, v(-0.76, -17.57) * mm, v(-0.83, -17.62) * mm, v(-0.9, -17.67) * mm, v(-0.9, -17.76) * mm, v(-0.87, -17.84) * mm, v(-0.85, -17.93) * mm, v(-0.84, -18) * mm, v(-0.83, -18.03) * mm]});
            skFitSpline(sketch, "E173", {"points": [v(-0.83, -18.03) * mm, v(-0.86, -18.02) * mm, v(-0.92, -18) * mm, v(-1, -17.98) * mm, v(-1.04, -17.97) * mm, v(-1.07, -17.96) * mm]});
            skFitSpline(sketch, "E174", {"points": [v(-1.07, -17.96) * mm, v(-1.06, -17.95) * mm, v(-1.06, -17.91) * mm, v(-1.05, -17.87) * mm, v(-1.04, -17.81) * mm, v(-1.14, -17.79) * mm, v(-1.12, -17.7) * mm, v(-1.13, -17.61) * mm, v(-1.16, -17.54) * mm, v(-1.2, -17.48) * mm, v(-1.19, -17.4) * mm, v(-1.13, -17.33) * mm, v(-1.16, -17.24) * mm, v(-1.14, -17.18) * mm, v(-1.13, -17.14) * mm, v(-1.14, -17.13) * mm, v(-1.15, -17.1) * mm, v(-1.2, -17.1) * mm, v(-1.24, -17.1) * mm, v(-1.28, -17.09) * mm, v(-1.3, -17.09) * mm]});
            skFitSpline(sketch, "E175", {"points": [v(-1.3, -17.09) * mm, v(-1.29, -17.07) * mm, v(-1.27, -17.03) * mm, v(-1.25, -16.98) * mm, v(-1.24, -16.95) * mm, v(-1.23, -16.93) * mm]});
            skFitSpline(sketch, "E176", {"points": [v(-1.23, -16.93) * mm, v(-1.24, -16.93) * mm, v(-1.26, -16.93) * mm, v(-1.3, -16.93) * mm, v(-1.33, -16.9) * mm, v(-1.34, -16.85) * mm, v(-1.38, -16.78) * mm, v(-1.38, -16.68) * mm, v(-1.4, -16.56) * mm, v(-1.51, -16.46) * mm, v(-1.6, -16.42) * mm, v(-1.65, -16.4) * mm]});
            skFitSpline(sketch, "E177", {"points": [v(-1.65, -16.4) * mm, v(-1.64, -16.37) * mm, v(-1.62, -16.31) * mm, v(-1.59, -16.23) * mm, v(-1.57, -16.18) * mm, v(-1.56, -16.15) * mm]});
            skFitSpline(sketch, "E178", {"points": [v(-1.56, -16.15) * mm, v(-1.64, -16.1) * mm, v(-1.8, -16) * mm, v(-1.94, -15.77) * mm, v(-1.96, -15.5) * mm, v(-1.95, -15.26) * mm, v(-1.96, -15.02) * mm, v(-2, -14.84) * mm, v(-2.03, -14.7) * mm, v(-2.04, -14.6) * mm, v(-2.04, -14.5) * mm, v(-2.04, -14.4) * mm, v(-2.1, -14.31) * mm, v(-2.16, -14.31) * mm, v(-2.2, -14.3) * mm]});
            skFitSpline(sketch, "E179", {"points": [v(-2.2, -14.3) * mm, v(-2.2, -14.3) * mm, v(-2.19, -14.26) * mm, v(-2.18, -14.23) * mm, v(-2.17, -14.18) * mm, v(-2.22, -14.14) * mm, v(-2.25, -14.07) * mm, v(-2.28, -14.04) * mm, v(-2.29, -14.02) * mm]});
            skFitSpline(sketch, "E180", {"points": [v(-2.29, -14.02) * mm, v(-2.32, -14) * mm, v(-2.38, -13.97) * mm, v(-2.46, -13.91) * mm, v(-2.54, -13.83) * mm, v(-2.6, -13.72) * mm, v(-2.68, -13.6) * mm, v(-2.77, -13.46) * mm, v(-2.9, -13.32) * mm, v(-3.02, -13.17) * mm, v(-3.15, -13.02) * mm, v(-3.29, -12.87) * mm, v(-3.42, -12.72) * mm, v(-3.54, -12.6) * mm, v(-3.63, -12.48) * mm, v(-3.7, -12.38) * mm, v(-3.8, -12.28) * mm, v(-3.89, -12.17) * mm, v(-3.99, -12.06) * mm, v(-4.05, -11.98) * mm, v(-4.08, -11.94) * mm]});
            skFitSpline(sketch, "E181", {"points": [v(-4.08, -11.94) * mm, v(-4.08, -11.94) * mm, v(-4.07, -11.93) * mm, v(-4.07, -11.93) * mm, v(-4.04, -11.9) * mm, v(-4.1, -11.92) * mm, v(-4.13, -11.92) * mm, v(-4.16, -11.93) * mm, v(-4.17, -11.93) * mm]});
            skFitSpline(sketch, "E182", {"points": [v(-4.17, -11.93) * mm, v(-4.18, -11.9) * mm, v(-4.2, -11.86) * mm, v(-4.22, -11.8) * mm, v(-4.28, -11.73) * mm, v(-4.38, -11.65) * mm, v(-4.49, -11.52) * mm, v(-4.5, -11.38) * mm, v(-4.52, -11.25) * mm, v(-4.61, -11.17) * mm, v(-4.68, -11.1) * mm, v(-4.72, -11.05) * mm, v(-4.77, -11.02) * mm, v(-4.8, -10.92) * mm, v(-4.76, -10.77) * mm, v(-4.84, -10.58) * mm, v(-4.94, -10.43) * mm, v(-5, -10.28) * mm, v(-4.95, -10.14) * mm, v(-4.93, -10.07) * mm, v(-4.92, -10.03) * mm]});
            skFitSpline(sketch, "E183", {"points": [v(-4.92, -10.03) * mm, v(-4.97, -9.98) * mm, v(-5.06, -9.9) * mm, v(-5.1, -9.7) * mm, v(-5.16, -9.6) * mm, v(-5.18, -9.54) * mm]});
            skFitSpline(sketch, "E184", {"points": [v(-9.68, -17.74) * mm, v(-9.72, -17.72) * mm, v(-9.8, -17.66) * mm, v(-9.94, -17.61) * mm, v(-10.02, -17.5) * mm, v(-10.07, -17.4) * mm, v(-10.12, -17.34) * mm, v(-10.17, -17.3) * mm, v(-10.18, -17.25) * mm, v(-10.18, -17.24) * mm, v(-10.2, -17.19) * mm, v(-10.29, -17.16) * mm, v(-10.38, -17.08) * mm, v(-10.46, -16.99) * mm, v(-10.51, -16.89) * mm, v(-10.6, -16.81) * mm, v(-10.68, -16.74) * mm, v(-10.77, -16.67) * mm, v(-10.85, -16.6) * mm, v(-10.93, -16.54) * mm, v(-11, -16.47) * mm, v(-11.08, -16.4) * mm, v(-11.14, -16.34) * mm, v(-11.2, -16.3) * mm, v(-11.24, -16.27) * mm, v(-11.28, -16.24) * mm, v(-11.31, -16.2) * mm, v(-11.34, -16.15) * mm, v(-11.4, -16.1) * mm, v(-11.47, -16.04) * mm, v(-11.55, -15.98) * mm, v(-11.65, -15.88) * mm, v(-11.74, -15.75) * mm, v(-11.85, -15.6) * mm, v(-11.95, -15.47) * mm, v(-12.03, -15.35) * mm, v(-12.1, -15.26) * mm, v(-12.15, -15.18) * mm, v(-12.2, -15.14) * mm, v(-12.22, -15.13) * mm, v(-12.25, -15.1) * mm, v(-12.27, -15.08) * mm, v(-12.3, -15.05) * mm, v(-12.32, -15) * mm, v(-12.36, -14.93) * mm, v(-12.4, -14.84) * mm, v(-12.43, -14.78) * mm, v(-12.44, -14.75) * mm]});
            skFitSpline(sketch, "E185", {"points": [v(-12.44, -14.75) * mm, v(-12.45, -14.76) * mm, v(-12.45, -14.76) * mm, v(-12.46, -14.76) * mm, v(-12.47, -14.77) * mm, v(-12.47, -14.77) * mm]});
            skFitSpline(sketch, "E186", {"points": [v(-12.47, -14.77) * mm, v(-12.48, -14.73) * mm, v(-12.5, -14.65) * mm, v(-12.53, -14.54) * mm, v(-12.5, -14.4) * mm, v(-12.56, -14.4) * mm, v(-12.6, -14.4) * mm, v(-12.62, -14.4) * mm, v(-12.64, -14.4) * mm]});
            skFitSpline(sketch, "E187", {"points": [v(-12.64, -14.4) * mm, v(-12.62, -14.32) * mm, v(-12.57, -14.18) * mm, v(-12.63, -13.95) * mm, v(-12.69, -13.82) * mm, v(-12.72, -13.75) * mm]});
            skFitSpline(sketch, "E188", {"points": [v(-12.72, -13.75) * mm, v(-12.69, -13.74) * mm, v(-12.63, -13.72) * mm, v(-12.6, -13.63) * mm, v(-12.67, -13.57) * mm, v(-12.75, -13.52) * mm, v(-12.75, -13.4) * mm, v(-12.76, -13.28) * mm, v(-12.8, -13.12) * mm, v(-12.8, -12.92) * mm, v(-12.8, -12.77) * mm, v(-12.8, -12.67) * mm, v(-12.81, -12.63) * mm, v(-12.82, -12.58) * mm, v(-12.85, -12.52) * mm, v(-12.86, -12.48) * mm, v(-12.9, -12.4) * mm, v(-12.87, -12.42) * mm, v(-12.85, -12.43) * mm, v(-12.84, -12.43) * mm, v(-12.83, -12.43) * mm]});
            skFitSpline(sketch, "E189", {"points": [v(-12.83, -12.43) * mm, v(-12.8, -12.42) * mm, v(-12.76, -12.4) * mm, v(-12.68, -12.36) * mm, v(-12.63, -12.34) * mm, v(-12.6, -12.32) * mm]});
            skFitSpline(sketch, "E190", {"points": [v(-12.6, -12.32) * mm, v(-12.66, -12.27) * mm, v(-12.78, -12.18) * mm, v(-12.85, -11.98) * mm, v(-12.86, -11.77) * mm, v(-12.8, -11.54) * mm, v(-12.68, -11.32) * mm, v(-12.5, -11.18) * mm, v(-12.4, -11.04) * mm, v(-12.36, -10.87) * mm, v(-12.2, -10.89) * mm, v(-12.2, -10.83) * mm, v(-12.2, -10.83) * mm, v(-12.18, -10.78) * mm, v(-12.1, -10.7) * mm, v(-12, -10.58) * mm, v(-11.88, -10.44) * mm, v(-11.71, -10.3) * mm, v(-11.51, -10.15) * mm, v(-11.37, -10.03) * mm, v(-11.26, -9.97) * mm, v(-11.2, -9.94) * mm, v(-11.13, -9.92) * mm, v(-11.05, -9.9) * mm, v(-10.96, -9.87) * mm, v(-10.87, -9.8) * mm, v(-10.77, -9.71) * mm, v(-10.6, -9.67) * mm, v(-10.5, -9.64) * mm, v(-10.44, -9.63) * mm]});
            skFitSpline(sketch, "E191", {"points": [v(-10.44, -9.63) * mm, v(-10.44, -9.66) * mm, v(-10.43, -9.72) * mm, v(-10.41, -9.81) * mm, v(-10.43, -9.92) * mm, v(-10.49, -10.05) * mm, v(-10.56, -10.2) * mm, v(-10.61, -10.32) * mm, v(-10.64, -10.4) * mm, v(-10.65, -10.44) * mm, v(-10.7, -10.55) * mm, v(-10.84, -10.7) * mm, v(-11.01, -10.94) * mm, v(-11.18, -11.16) * mm, v(-11.31, -11.38) * mm, v(-11.44, -11.58) * mm, v(-11.54, -11.74) * mm, v(-11.6, -11.85) * mm, v(-11.65, -11.92) * mm, v(-11.68, -11.97) * mm, v(-11.7, -12) * mm]});
            skFitSpline(sketch, "E192", {"points": [v(-11.7, -12) * mm, v(-11.68, -12.02) * mm, v(-11.67, -12.06) * mm, v(-11.66, -12.14) * mm, v(-11.72, -12.25) * mm, v(-11.8, -12.4) * mm, v(-11.79, -12.65) * mm, v(-11.74, -12.88) * mm, v(-11.67, -13.13) * mm, v(-11.57, -13.38) * mm, v(-11.46, -13.63) * mm, v(-11.35, -13.87) * mm, v(-11.22, -14.1) * mm, v(-11.11, -14.3) * mm, v(-11.03, -14.45) * mm, v(-10.97, -14.56) * mm, v(-10.9, -14.66) * mm, v(-10.88, -14.76) * mm, v(-10.87, -14.85) * mm, v(-10.81, -14.9) * mm, v(-10.77, -14.94) * mm, v(-10.76, -15) * mm, v(-10.74, -15.1) * mm, v(-10.7, -15.29) * mm, v(-10.61, -15.52) * mm, v(-10.5, -15.72) * mm, v(-10.44, -15.89) * mm, v(-10.4, -16.03) * mm, v(-10.33, -16.19) * mm, v(-10.22, -16.34) * mm, v(-10.11, -16.5) * mm, v(-9.98, -16.65) * mm, v(-9.86, -16.77) * mm, v(-9.78, -16.92) * mm, v(-9.77, -17.03) * mm, v(-9.77, -17.09) * mm]});
            skFitSpline(sketch, "E193", {"points": [v(-9, -17.2) * mm, v(-8.99, -17.19) * mm, v(-8.96, -17.17) * mm, v(-8.94, -17.15) * mm, v(-8.89, -17.11) * mm, v(-8.82, -17.21) * mm, v(-8.72, -17.25) * mm, v(-8.65, -17.35) * mm, v(-8.65, -17.48) * mm, v(-8.51, -17.54) * mm, v(-8.43, -17.54) * mm, v(-8.38, -17.54) * mm]});
            skFitSpline(sketch, "E194", {"points": [v(-8.38, -17.54) * mm, v(-8.39, -17.57) * mm, v(-8.4, -17.64) * mm, v(-8.28, -17.76) * mm, v(-8.4, -17.77) * mm, v(-8.48, -17.77) * mm]});
            skFitSpline(sketch, "E195", {"points": [v(-8.48, -17.77) * mm, v(-8.47, -17.8) * mm, v(-8.44, -17.85) * mm, v(-8.5, -17.93) * mm, v(-8.61, -17.9) * mm, v(-8.75, -17.89) * mm, v(-8.93, -17.85) * mm, v(-9.08, -17.82) * mm, v(-9.2, -17.8) * mm, v(-9.3, -17.79) * mm, v(-9.4, -17.75) * mm, v(-9.49, -17.7) * mm, v(-9.6, -17.69) * mm, v(-9.65, -17.73) * mm, v(-9.68, -17.74) * mm]});
            skFitSpline(sketch, "E196", {"points": [v(3.2, -0.11) * mm, v(3.2, -0.13) * mm, v(3.22, -0.16) * mm, v(3.25, -0.2) * mm, v(3.27, -0.24) * mm, v(3.26, -0.29) * mm, v(3.26, -0.33) * mm, v(3.25, -0.37) * mm, v(3.25, -0.38) * mm]});
            skFitSpline(sketch, "E197", {"points": [v(3.25, -0.38) * mm, v(3.23, -0.38) * mm, v(3.2, -0.37) * mm, v(3.17, -0.37) * mm, v(3.13, -0.35) * mm, v(3.1, -0.31) * mm, v(3.08, -0.27) * mm, v(3.05, -0.23) * mm, v(3.03, -0.2) * mm, v(3.02, -0.18) * mm, v(2.97, -0.15) * mm, v(2.86, -0.22) * mm, v(2.76, -0.1) * mm, v(2.66, 0) * mm, v(2.5, 0.1) * mm, v(2.33, 0.21) * mm, v(2.18, 0.3) * mm, v(2.08, 0.36) * mm, v(2.02, 0.4) * mm, v(1.94, 0.44) * mm, v(1.84, 0.48) * mm, v(1.72, 0.52) * mm, v(1.62, 0.56) * mm, v(1.54, 0.61) * mm, v(1.48, 0.67) * mm, v(1.37, 0.73) * mm, v(1.23, 0.77) * mm, v(1.06, 0.82) * mm, v(0.9, 0.89) * mm, v(0.76, 0.98) * mm, v(0.64, 1.08) * mm, v(0.55, 1.22) * mm, v(0.5, 1.39) * mm, v(0.47, 1.58) * mm, v(0.52, 1.72) * mm, v(0.54, 1.8) * mm, v(0.54, 1.82) * mm, v(0.54, 1.86) * mm, v(0.53, 1.9) * mm, v(0.52, 1.96) * mm, v(0.54, 2.02) * mm, v(0.6, 2.05) * mm, v(0.65, 2.09) * mm, v(0.75, 2.1) * mm, v(0.88, 2.07) * mm, v(1.03, 2.04) * mm, v(1.18, 2) * mm, v(1.32, 1.93) * mm, v(1.45, 1.86) * mm, v(1.6, 1.79) * mm, v(1.77, 1.72) * mm, v(1.96, 1.66) * mm, v(2.13, 1.6) * mm, v(2.27, 1.53) * mm, v(2.38, 1.47) * mm, v(2.5, 1.43) * mm, v(2.64, 1.41) * mm, v(2.78, 1.37) * mm, v(2.85, 1.3) * mm, v(2.9, 1.26) * mm, v(2.92, 1.26) * mm, v(2.95, 1.25) * mm, v(2.98, 1.25) * mm, v(3.02, 1.25) * mm, v(3.04, 1.25) * mm, v(3.05, 1.25) * mm]});
            skFitSpline(sketch, "E198", {"points": [v(3.05, 1.25) * mm, v(3.05, 1.24) * mm, v(3.04, 1.21) * mm, v(3.03, 1.18) * mm, v(3.03, 1.16) * mm, v(3.03, 1.14) * mm]});
            skFitSpline(sketch, "E199", {"points": [v(3.03, 1.14) * mm, v(3.05, 1.15) * mm, v(3.1, 1.16) * mm, v(3.18, 1.2) * mm, v(3.3, 1.18) * mm, v(3.44, 1.11) * mm, v(3.62, 1.1) * mm, v(3.77, 1.1) * mm, v(3.88, 1.08) * mm, v(3.95, 1.06) * mm, v(4.02, 1.04) * mm, v(4.09, 1.01) * mm, v(4.15, 0.97) * mm, v(4.19, 0.95) * mm, v(4.21, 0.93) * mm]});
            skFitSpline(sketch, "E200", {"points": [v(4.21, 0.93) * mm, v(4.2, 0.88) * mm, v(4.14, 0.76) * mm, v(4.07, 0.58) * mm, v(4.02, 0.46) * mm, v(4, 0.4) * mm]});
            skFitSpline(sketch, "E201", {"points": [v(4, 0.4) * mm, v(4, 0.38) * mm, v(3.99, 0.36) * mm, v(4, 0.33) * mm, v(4.01, 0.26) * mm, v(4, 0.16) * mm, v(4, 0.02) * mm, v(3.99, -0.07) * mm, v(3.98, -0.12) * mm]});
            skFitSpline(sketch, "E202", {"points": [v(3.98, -0.12) * mm, v(3.97, -0.11) * mm, v(3.94, -0.11) * mm, v(3.9, -0.11) * mm, v(3.88, -0.1) * mm, v(3.86, -0.1) * mm]});
            skFitSpline(sketch, "E203", {"points": [v(3.86, -0.1) * mm, v(3.86, -0.13) * mm, v(3.84, -0.18) * mm, v(3.82, -0.26) * mm, v(3.8, -0.3) * mm, v(3.8, -0.33) * mm]});
            skFitSpline(sketch, "E204", {"points": [v(3.8, -0.33) * mm, v(3.81, -0.35) * mm, v(3.84, -0.38) * mm, v(3.9, -0.47) * mm, v(3.79, -0.47) * mm, v(3.77, -0.52) * mm, v(3.77, -0.54) * mm, v(3.77, -0.58) * mm, v(3.86, -0.57) * mm, v(3.8, -0.62) * mm, v(3.8, -0.65) * mm, v(3.8, -0.66) * mm]});
            skFitSpline(sketch, "E205", {"points": [v(3.8, -0.66) * mm, v(3.78, -0.66) * mm, v(3.75, -0.66) * mm, v(3.71, -0.66) * mm, v(3.66, -0.63) * mm, v(3.6, -0.56) * mm, v(3.54, -0.46) * mm, v(3.57, -0.35) * mm, v(3.61, -0.28) * mm, v(3.64, -0.2) * mm, v(3.55, -0.19) * mm, v(3.56, -0.13) * mm, v(3.57, -0.1) * mm, v(3.58, -0.06) * mm, v(3.62, -0.03) * mm, v(3.66, 0) * mm, v(3.69, 0.03) * mm, v(3.7, 0.05) * mm]});
            skFitSpline(sketch, "E206", {"points": [v(3.7, 0.05) * mm, v(3.67, 0.05) * mm, v(3.62, 0.06) * mm, v(3.55, 0.08) * mm, v(3.52, 0.08) * mm, v(3.5, 0.09) * mm]});
            skFitSpline(sketch, "E207", {"points": [v(3.5, 0.09) * mm, v(3.49, 0.06) * mm, v(3.47, 0) * mm, v(3.43, -0.07) * mm, v(3.41, -0.12) * mm, v(3.4, -0.14) * mm]});
            skFitSpline(sketch, "E208", {"points": [v(3.4, -0.14) * mm, v(3.38, -0.14) * mm, v(3.34, -0.13) * mm, v(3.26, -0.12) * mm, v(3.22, -0.12) * mm, v(3.2, -0.11) * mm]});
            skFitSpline(sketch, "E209", {"points": [v(13.33, -11.07) * mm, v(13.32, -11.13) * mm, v(13.31, -11.23) * mm, v(13.24, -11.36) * mm, v(13.13, -11.42) * mm, v(13, -11.42) * mm, v(12.88, -11.37) * mm, v(12.83, -11.28) * mm, v(12.78, -11.2) * mm, v(12.73, -11.17) * mm, v(12.63, -11.1) * mm, v(12.5, -11) * mm, v(12.31, -10.87) * mm, v(12.16, -10.77) * mm, v(12.08, -10.67) * mm, v(12.06, -10.63) * mm, v(12.06, -10.62) * mm]});
            skFitSpline(sketch, "E210", {"points": [v(12.06, -10.62) * mm, v(12.05, -10.6) * mm, v(12.05, -10.52) * mm, v(12.09, -10.42) * mm, v(12.17, -10.33) * mm, v(12.3, -10.3) * mm, v(12.39, -10.31) * mm, v(12.46, -10.34) * mm, v(12.51, -10.36) * mm, v(12.61, -10.42) * mm, v(12.75, -10.51) * mm, v(12.94, -10.63) * mm, v(13.1, -10.73) * mm, v(13.24, -10.83) * mm, v(13.31, -10.95) * mm, v(13.32, -11.03) * mm, v(13.33, -11.07) * mm]});
            skFitSpline(sketch, "E211", {"points": [v(9.3, -2.6) * mm, v(9.3, -2.6) * mm, v(9.3, -2.59) * mm, v(9.3, -2.58) * mm, v(9.33, -2.56) * mm, v(9.37, -2.64) * mm, v(9.44, -2.68) * mm, v(9.5, -2.72) * mm, v(9.51, -2.77) * mm, v(9.52, -2.81) * mm, v(9.52, -2.84) * mm, v(9.52, -2.85) * mm]});
            skFitSpline(sketch, "E212", {"points": [v(9.52, -2.85) * mm, v(9.5, -2.85) * mm, v(9.48, -2.84) * mm, v(9.43, -2.83) * mm, v(9.39, -2.8) * mm, v(9.36, -2.74) * mm, v(9.33, -2.67) * mm, v(9.3, -2.62) * mm, v(9.3, -2.6) * mm]});
            skFitSpline(sketch, "E213", {"points": [v(-10.67, -8.25) * mm, v(-10.68, -8.26) * mm, v(-10.69, -8.28) * mm, v(-10.7, -8.32) * mm, v(-10.72, -8.34) * mm, v(-10.72, -8.35) * mm]});
            skFitSpline(sketch, "E214", {"points": [v(-10.72, -8.35) * mm, v(-10.75, -8.33) * mm, v(-10.8, -8.3) * mm, v(-10.85, -8.24) * mm, v(-10.95, -8.22) * mm, v(-10.92, -8.17) * mm, v(-10.91, -8.16) * mm, v(-10.9, -8.11) * mm, v(-10.82, -8.2) * mm, v(-10.75, -8.21) * mm, v(-10.7, -8.24) * mm, v(-10.67, -8.25) * mm]});
            skFitSpline(sketch, "E215", {"points": [v(-2.52, 2.65) * mm, v(-2.52, 2.64) * mm, v(-2.52, 2.63) * mm, v(-2.52, 2.6) * mm, v(-2.53, 2.6) * mm, v(-2.53, 2.6) * mm]});
            skFitSpline(sketch, "E216", {"points": [v(-2.53, 2.6) * mm, v(-2.56, 2.6) * mm, v(-2.62, 2.6) * mm, v(-2.72, 2.62) * mm, v(-2.78, 2.63) * mm, v(-2.81, 2.63) * mm]});
            skFitSpline(sketch, "E217", {"points": [v(-2.81, 2.63) * mm, v(-2.81, 2.64) * mm, v(-2.8, 2.66) * mm, v(-2.8, 2.68) * mm, v(-2.8, 2.7) * mm, v(-2.8, 2.7) * mm]});
            skFitSpline(sketch, "E218", {"points": [v(-2.8, 2.7) * mm, v(-2.77, 2.7) * mm, v(-2.7, 2.69) * mm, v(-2.61, 2.67) * mm, v(-2.55, 2.65) * mm, v(-2.52, 2.65) * mm]});
            skLineSegment(sketch, "E219", {"start": v(-9.77, -17.09) * mm, "end": v(-9, -17.2) * mm});
            skSolve(sketch);
        }
        {
            var Q0;
            Q0 = qSketchRegion(id + "F0", true);
            var Q1;
            Q1=makeQuery(id+"F0.imprint","IMPRINT",FACE,{"disambiguationData":[TD([[makeQuery(id+"F0.imprint","IMPRINT",EDGE,{"derivedFrom":sQuery(id+"F0.wireOp",EDGE,"E4")}),1.0]])]});
            var Q2;
            Q2=makeQuery(id+"F0.imprint","IMPRINT",FACE,{"disambiguationData":[TD([[makeQuery(id+"F0.imprint","IMPRINT",EDGE,{"derivedFrom":sQuery(id+"F0.wireOp",EDGE,"E9")}),-1.0]])]});
            var Q3;
            Q3=makeQuery(id+"F0.imprint","IMPRINT",FACE,{"disambiguationData":[TD([[makeQuery(id+"F0.imprint","IMPRINT",EDGE,{"derivedFrom":sQuery(id+"F0.wireOp",EDGE,"E209")}),-1.0]])]});
            var Q4;
            Q4=makeQuery(id+"F0.imprint","IMPRINT",FACE,{"disambiguationData":[TD([[makeQuery(id+"F0.imprint","IMPRINT",EDGE,{"derivedFrom":sQuery(id+"F0.wireOp",EDGE,"E196")}),-1.0]])]});
            var Q5;
            Q5=makeQuery(id+"F0.imprint","IMPRINT",FACE,{"disambiguationData":[TD([[makeQuery(id+"F0.imprint","IMPRINT",EDGE,{"derivedFrom":sQuery(id+"F0.wireOp",EDGE,"E211")}),-1.0]])]});
            var Q6;
            Q6=makeQuery(id+"F0.imprint","IMPRINT",FACE,{"disambiguationData":[TD([[makeQuery(id+"F0.imprint","IMPRINT",EDGE,{"derivedFrom":sQuery(id+"F0.wireOp",EDGE,"E215")}),-1.0]])]});
            var Q7;
            {var subQ0=sQuery(id+"F0.wireOp",EDGE,"4f91bc52-ea37-4763-9065-8550c5facef6");Q7=makeQuery(id+"F0.imprint","IMPRINT",FACE,{"disambiguationData":[TD([[makeQuery(id+"F0.imprint","IMPRINT",EDGE,{"derivedFrom":subQ0}),-1.0]])]});}
            var Q8;
            Q8=makeQuery(id+"F0.imprint","IMPRINT",FACE,{"disambiguationData":[TD([[makeQuery(id+"F0.imprint","IMPRINT",EDGE,{"derivedFrom":sQuery(id+"F0.wireOp",EDGE,"E213")}),-1.0]])]});
            var Q9;
            Q9=makeQuery(id+"F0.imprint","IMPRINT",FACE,{"disambiguationData":[TD([[makeQuery(id+"F0.imprint","IMPRINT",EDGE,{"derivedFrom":sQuery(id+"F0.wireOp",EDGE,"E184")}),-1.0]])]});
            extrude(context, id + "F1", {"entities" : qUnion([Q0, Q1, Q2, Q3, Q4, Q5, Q6, Q7, Q8, Q9]), "oppositeDirection" : true, "depth" : 5 * mm, "offsetDistance" : 25 * mm});
        }
        {
            var Q0;
            Q0=makeQuery(id+"F0.imprint","IMPRINT",FACE,{"disambiguationData":[TD([[makeQuery(id+"F0.imprint","IMPRINT",EDGE,{"derivedFrom":sQuery(id+"F0.wireOp",EDGE,"E4")}),1.0]])]});
            extrude(context, id + "F2", {"entities" : qUnion([Q0]), "operationType" : NewBodyOperationType.ADD, "depth" : 1 * mm, "offsetDistance" : 25 * mm});
        }
    });
